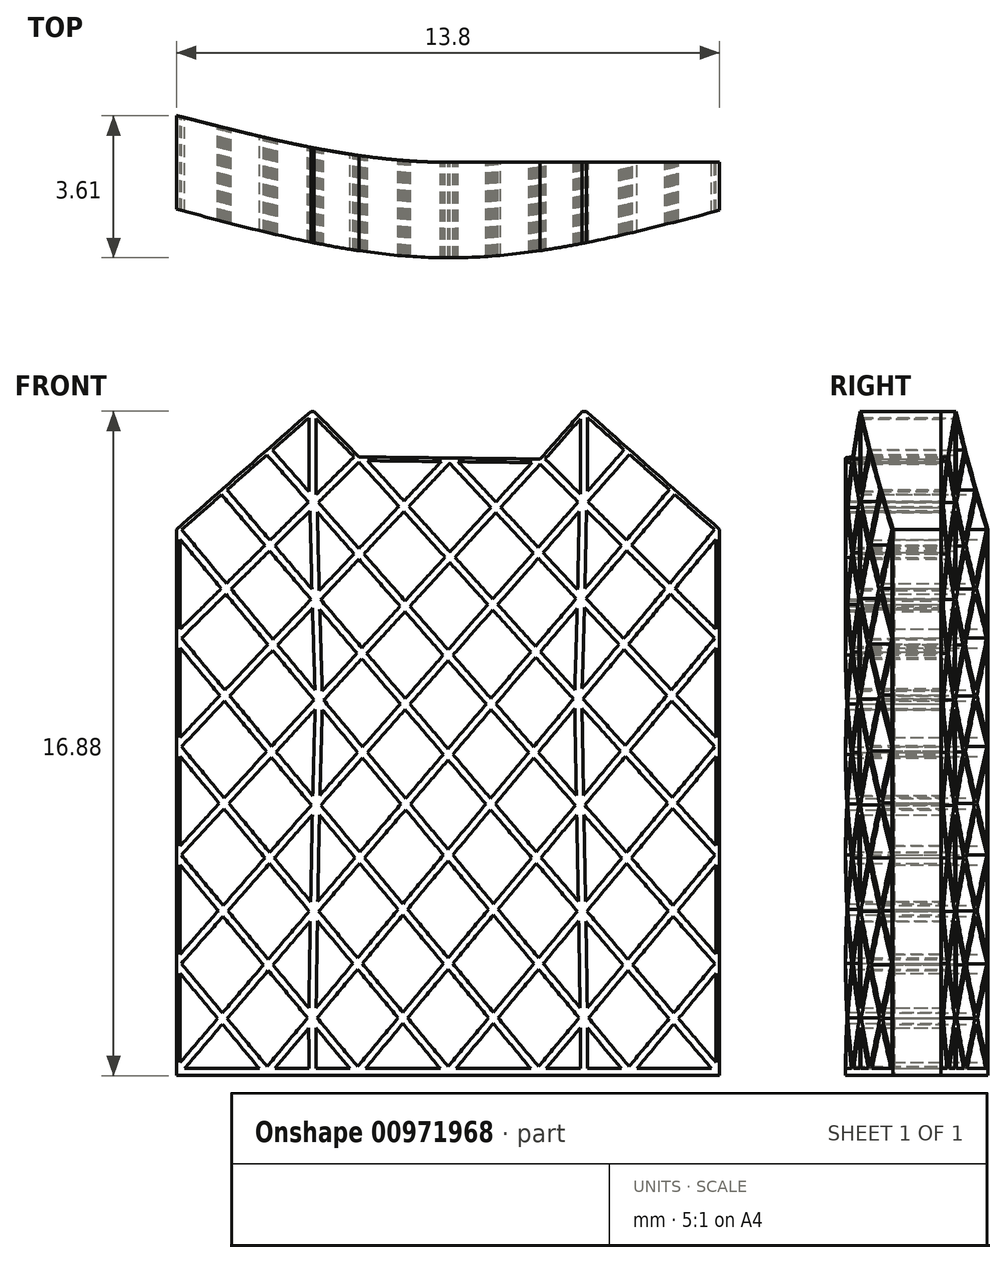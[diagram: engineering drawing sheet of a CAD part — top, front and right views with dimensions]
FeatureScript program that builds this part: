
annotation { "Feature Type Name" : "Feature", "Feature Type Description" : "" }
export const myFeature = defineFeature(function(context is Context, id is Id, definition is map)
    precondition{}
    {
        {
            var Q0;
            Q0=qCreatedBy(makeId("Top.planeOp"),FACE);
            var sketch = newSketch(context, id + "F0", { "sketchPlane" : qUnion([Q0])});
            skLineSegment(sketch, "E0", {"start": v(0, -22.65) * mm, "end": v(38.1, -22.65) * mm});
            skLineSegment(sketch, "E1", {"start": v(38.1, -22.65) * mm, "end": v(-38.1, -22.65) * mm});
            skLineSegment(sketch, "E2", {"start": v(38.1, -22.65) * mm, "end": v(38.1, -16.26) * mm});
            skLineSegment(sketch, "E3", {"start": v(38.1, -16.26) * mm, "end": v(38.1, -29.4) * mm});
            skLineSegment(sketch, "E4", {"start": v(-38.1, -22.65) * mm, "end": v(-38.1, -29.22) * mm});
            skLineSegment(sketch, "E5", {"start": v(-38.1, -29.22) * mm, "end": v(-38.1, -16.09) * mm});
            skPoint(sketch, "E6", {"position": v(-38.1, -22.65) * mm});
            skPoint(sketch, "E7", {"position": v(38.1, -22.82) * mm});
            skFitSpline(sketch, "E8", {"points": [v(-38.1, -16.09) * mm, v(0, -22.65) * mm, v(38.1, -16.26) * mm], "startDerivative": vector(76.18, -19.61) * mm, "endDerivative": vector(76.22, 19.27) * mm});
            skLineSegment(sketch, "E9", {"start": v(0, -22.65) * mm, "end": v(0, -36.06) * mm});
            skFitSpline(sketch, "E10", {"points": [v(-38.1, -29.22) * mm, v(0, -36.06) * mm, v(38.1, -29.4) * mm], "startDerivative": vector(76.18, -20.42) * mm, "endDerivative": vector(76.22, 20.08) * mm});
            skSolve(sketch);
        }
        {
            var Q0;
            Q0=qCreatedBy(makeId("Front.planeOp"),FACE);
            var sketch = newSketch(context, id + "F1", { "sketchPlane" : qUnion([Q0])});
            skLineSegment(sketch, "E11", {"start": v(38.1, -46.14) * mm, "end": v(25.4, -46.14) * mm, "construction": true});
            skLineSegment(sketch, "E12", {"start": v(-38.1, -46.14) * mm, "end": v(-38.1, -30.9) * mm, "construction": true});
            skLineSegment(sketch, "E13", {"start": v(38.1, 30.06) * mm, "end": v(38.1, 14.82) * mm, "construction": true});
            skLineSegment(sketch, "E14", {"start": v(-38.1, 30.06) * mm, "end": v(-31.74, 35.65) * mm, "construction": true});
            skLineSegment(sketch, "E15", {"start": v(38.1, 30.06) * mm, "end": v(31.76, 35.67) * mm, "construction": true});
            skLineSegment(sketch, "E16", {"start": v(-19.02, 46.83) * mm, "end": v(-12.48, 40.22) * mm, "construction": true});
            skLineSegment(sketch, "E17", {"start": v(19.08, 46.9) * mm, "end": v(12.92, 39.93) * mm, "construction": true});
            skLineSegment(sketch, "E18", {"start": v(-12.48, 40.22) * mm, "end": v(0.22, 40.07) * mm, "construction": true});
            skLineSegment(sketch, "E19", {"start": v(-25.38, 41.24) * mm, "end": v(-19.02, 46.83) * mm, "construction": true});
            skLineSegment(sketch, "E20", {"start": v(-31.74, 35.65) * mm, "end": v(-25.38, 41.24) * mm, "construction": true});
            skLineSegment(sketch, "E21", {"start": v(25.42, 41.28) * mm, "end": v(19.08, 46.9) * mm, "construction": true});
            skLineSegment(sketch, "E22", {"start": v(31.76, 35.67) * mm, "end": v(25.42, 41.28) * mm, "construction": true});
            skLineSegment(sketch, "E23", {"start": v(38.1, 14.82) * mm, "end": v(38.1, -0.42) * mm, "construction": true});
            skLineSegment(sketch, "E24", {"start": v(38.1, -0.42) * mm, "end": v(38.1, -15.66) * mm, "construction": true});
            skLineSegment(sketch, "E25", {"start": v(38.1, -15.66) * mm, "end": v(38.1, -30.9) * mm, "construction": true});
            skLineSegment(sketch, "E26", {"start": v(38.1, -30.9) * mm, "end": v(38.1, -46.14) * mm, "construction": true});
            skLineSegment(sketch, "E27", {"start": v(-38.1, 14.82) * mm, "end": v(-38.1, 30.06) * mm, "construction": true});
            skLineSegment(sketch, "E28", {"start": v(-38.1, -0.42) * mm, "end": v(-38.1, 14.82) * mm, "construction": true});
            skLineSegment(sketch, "E29", {"start": v(-38.1, -15.66) * mm, "end": v(-38.1, -0.42) * mm, "construction": true});
            skLineSegment(sketch, "E30", {"start": v(-38.1, -30.9) * mm, "end": v(-38.1, -15.66) * mm, "construction": true});
            skLineSegment(sketch, "E31", {"start": v(-25.4, -46.14) * mm, "end": v(-38.1, -46.14) * mm, "construction": true});
            skLineSegment(sketch, "E32", {"start": v(-12.7, -46.14) * mm, "end": v(-19.02, -46.14) * mm, "construction": true});
            skLineSegment(sketch, "E33", {"start": v(-50.8, 0) * mm, "end": v(-50.8, 0) * mm});
            skLineSegment(sketch, "E34", {"start": v(12.7, -46.14) * mm, "end": v(0, -46.14) * mm, "construction": true});
            skLineSegment(sketch, "E35", {"start": v(25.4, -46.14) * mm, "end": v(19.08, -46.14) * mm, "construction": true});
            skLineSegment(sketch, "E36", {"start": v(0, -46.14) * mm, "end": v(-12.7, -46.14) * mm, "construction": true});
            skLineSegment(sketch, "E37", {"start": v(12.92, 39.93) * mm, "end": v(18.94, 33.92) * mm, "construction": true});
            skPoint(sketch, "E38", {"position": v(0.22, 40.07) * mm});
            skLineSegment(sketch, "E39", {"start": v(-12.48, 40.22) * mm, "end": v(-6.2, 33.29) * mm, "construction": true});
            skLineSegment(sketch, "E40", {"start": v(0.22, 40.07) * mm, "end": v(6.7, 33.15) * mm, "construction": true});
            skLineSegment(sketch, "E41", {"start": v(-25.38, 41.24) * mm, "end": v(-19.02, 34.01) * mm, "construction": true});
            skLineSegment(sketch, "E42", {"start": v(-31.74, 35.65) * mm, "end": v(-25.02, 27.78) * mm, "construction": true});
            skLineSegment(sketch, "E43", {"start": v(-38.1, 30.06) * mm, "end": v(-31.15, 21.71) * mm, "construction": true});
            skLineSegment(sketch, "E44", {"start": v(-38.1, -0.42) * mm, "end": v(-31.44, -8.4) * mm, "construction": true});
            skLineSegment(sketch, "E45", {"start": v(-38.1, -15.66) * mm, "end": v(-31.58, -23.49) * mm, "construction": true});
            skLineSegment(sketch, "E46", {"start": v(-38.1, -30.9) * mm, "end": v(-31.67, -38.62) * mm, "construction": true});
            skLineSegment(sketch, "E47", {"start": v(-12.48, 40.22) * mm, "end": v(-18.9, 33.86) * mm, "construction": true});
            skLineSegment(sketch, "E48", {"start": v(0.22, 40.07) * mm, "end": v(-6.2, 33.29) * mm, "construction": true});
            skLineSegment(sketch, "E49", {"start": v(12.92, 39.93) * mm, "end": v(6.7, 33.15) * mm, "construction": true});
            skLineSegment(sketch, "E50", {"start": v(25.42, 41.28) * mm, "end": v(19.08, 34.07) * mm, "construction": true});
            skLineSegment(sketch, "E51", {"start": v(31.76, 35.67) * mm, "end": v(25.06, 27.82) * mm, "construction": true});
            skLineSegment(sketch, "E52", {"start": v(38.1, 30.06) * mm, "end": v(31.16, 21.73) * mm, "construction": true});
            skLineSegment(sketch, "E53", {"start": v(38.1, 14.82) * mm, "end": v(31.38, 6.76) * mm, "construction": true});
            skLineSegment(sketch, "E54", {"start": v(38.1, -0.42) * mm, "end": v(31.49, -8.36) * mm, "construction": true});
            skLineSegment(sketch, "E55", {"start": v(38.1, -30.9) * mm, "end": v(31.67, -38.61) * mm, "construction": true});
            skLineSegment(sketch, "E56", {"start": v(-38.1, 14.82) * mm, "end": v(-31.35, 6.71) * mm, "construction": true});
            skLineSegment(sketch, "E57", {"start": v(38.1, -15.66) * mm, "end": v(31.58, -23.49) * mm, "construction": true});
            skLineSegment(sketch, "E58", {"start": v(0.22, 40.07) * mm, "end": v(12.92, 39.93) * mm, "construction": true});
            skLineSegment(sketch, "E59", {"start": v(19.08, 34.07) * mm, "end": v(18.94, 33.92) * mm, "construction": true});
            skLineSegment(sketch, "E60", {"start": v(18.94, 33.92) * mm, "end": v(19.08, 33.79) * mm, "construction": true});
            skLineSegment(sketch, "E61", {"start": v(19.08, 33.79) * mm, "end": v(25.06, 27.82) * mm, "construction": true});
            skLineSegment(sketch, "E62", {"start": v(18.67, 20.34) * mm, "end": v(12.28, 12.86) * mm, "construction": true});
            skLineSegment(sketch, "E63", {"start": v(18.53, -8.66) * mm, "end": v(12.4, -16.03) * mm, "construction": true});
            skLineSegment(sketch, "E64", {"start": v(18.82, -23.56) * mm, "end": v(12.7, -30.9) * mm, "construction": true});
            skLineSegment(sketch, "E65", {"start": v(19.08, -46.14) * mm, "end": v(12.7, -46.14) * mm, "construction": true});
            skLineSegment(sketch, "E66", {"start": v(18.94, 33.92) * mm, "end": v(12.66, 26.78) * mm, "construction": true});
            skLineSegment(sketch, "E67", {"start": v(25.06, 27.82) * mm, "end": v(18.67, 20.34) * mm, "construction": true});
            skLineSegment(sketch, "E68", {"start": v(25.06, 27.82) * mm, "end": v(31.16, 21.73) * mm, "construction": true});
            skLineSegment(sketch, "E69", {"start": v(31.16, 21.73) * mm, "end": v(24.67, 13.94) * mm, "construction": true});
            skLineSegment(sketch, "E70", {"start": v(31.16, 21.73) * mm, "end": v(38.1, 14.82) * mm, "construction": true});
            skLineSegment(sketch, "E71.0", {"start": v(24.7, 41.23) * mm, "end": v(19.59, 45.76) * mm});
            skLineSegment(sketch, "E71.1", {"start": v(24.7, 41.23) * mm, "end": v(19.59, 35.43) * mm});
            skLineSegment(sketch, "E71.2", {"start": v(19.59, 45.76) * mm, "end": v(19.59, 35.43) * mm});
            skLineSegment(sketch, "E72.0", {"start": v(18.56, 45.52) * mm, "end": v(18.56, 35.03) * mm});
            skLineSegment(sketch, "E72.1", {"start": v(18.56, 45.52) * mm, "end": v(13.63, 39.95) * mm});
            skLineSegment(sketch, "E72.2", {"start": v(13.63, 39.95) * mm, "end": v(18.56, 35.03) * mm});
            skLineSegment(sketch, "E73.0", {"start": v(31.05, 35.62) * mm, "end": v(25.46, 40.56) * mm});
            skLineSegment(sketch, "E73.1", {"start": v(31.05, 35.62) * mm, "end": v(25.03, 28.57) * mm});
            skLineSegment(sketch, "E73.2", {"start": v(19.64, 33.94) * mm, "end": v(25.03, 28.57) * mm});
            skLineSegment(sketch, "E73.3", {"start": v(25.46, 40.56) * mm, "end": v(19.64, 33.94) * mm});
            skLineSegment(sketch, "E74.0", {"start": v(37.4, 30) * mm, "end": v(31.8, 34.95) * mm});
            skLineSegment(sketch, "E74.1", {"start": v(37.4, 30) * mm, "end": v(31.13, 22.49) * mm});
            skLineSegment(sketch, "E74.2", {"start": v(25.75, 27.85) * mm, "end": v(31.13, 22.49) * mm});
            skLineSegment(sketch, "E74.3", {"start": v(31.8, 34.95) * mm, "end": v(25.75, 27.85) * mm});
            skLineSegment(sketch, "E75.0", {"start": v(37.6, 28.65) * mm, "end": v(37.6, 16.04) * mm});
            skLineSegment(sketch, "E75.1", {"start": v(37.6, 28.65) * mm, "end": v(31.85, 21.77) * mm});
            skLineSegment(sketch, "E75.2", {"start": v(31.85, 21.77) * mm, "end": v(37.6, 16.04) * mm});
            skLineSegment(sketch, "E76", {"start": v(-19.02, 34.01) * mm, "end": v(-18.9, 33.86) * mm, "construction": true});
            skLineSegment(sketch, "E77", {"start": v(-18.9, 33.86) * mm, "end": v(-19.02, 33.73) * mm, "construction": true});
            skLineSegment(sketch, "E78", {"start": v(-18.9, 33.86) * mm, "end": v(-12.52, 26.62) * mm, "construction": true});
            skLineSegment(sketch, "E79", {"start": v(-19.02, 33.73) * mm, "end": v(-25.02, 27.78) * mm, "construction": true});
            skLineSegment(sketch, "E80", {"start": v(-18.57, 20.22) * mm, "end": v(-12.1, 12.66) * mm, "construction": true});
            skLineSegment(sketch, "E81", {"start": v(-18.57, 20.22) * mm, "end": v(-24.6, 13.85) * mm, "construction": true});
            skLineSegment(sketch, "E82", {"start": v(-18.13, 6.1) * mm, "end": v(-12, -1.25) * mm, "construction": true});
            skLineSegment(sketch, "E83", {"start": v(-18.13, 6.1) * mm, "end": v(-24.79, -1.16) * mm, "construction": true});
            skLineSegment(sketch, "E84", {"start": v(-18.82, -23.56) * mm, "end": v(-12.7, -30.9) * mm, "construction": true});
            skLineSegment(sketch, "E85", {"start": v(-18.82, -23.56) * mm, "end": v(-25.25, -31.09) * mm, "construction": true});
            skLineSegment(sketch, "E86", {"start": v(-19.05, -38.52) * mm, "end": v(-12.7, -46.14) * mm, "construction": true});
            skLineSegment(sketch, "E87", {"start": v(-19.05, -38.52) * mm, "end": v(-25.4, -46.14) * mm, "construction": true});
            skLineSegment(sketch, "E88", {"start": v(-19.02, -46.14) * mm, "end": v(-25.4, -46.14) * mm, "construction": true});
            skLineSegment(sketch, "E89", {"start": v(-25.02, 27.78) * mm, "end": v(-18.57, 20.22) * mm, "construction": true});
            skLineSegment(sketch, "E90", {"start": v(-25.02, 27.78) * mm, "end": v(-31.15, 21.71) * mm, "construction": true});
            skLineSegment(sketch, "E91", {"start": v(-31.15, 21.71) * mm, "end": v(-24.6, 13.85) * mm, "construction": true});
            skLineSegment(sketch, "E92", {"start": v(-31.15, 21.71) * mm, "end": v(-38.1, 14.82) * mm, "construction": true});
            skLineSegment(sketch, "E93.0", {"start": v(-37.4, 30) * mm, "end": v(-31.8, 34.93) * mm});
            skLineSegment(sketch, "E93.1", {"start": v(-37.4, 30) * mm, "end": v(-31.11, 22.46) * mm});
            skLineSegment(sketch, "E93.2", {"start": v(-25.72, 27.81) * mm, "end": v(-31.11, 22.46) * mm});
            skLineSegment(sketch, "E93.3", {"start": v(-31.8, 34.93) * mm, "end": v(-25.72, 27.81) * mm});
            skLineSegment(sketch, "E94.0", {"start": v(-37.6, 28.65) * mm, "end": v(-31.83, 21.75) * mm});
            skLineSegment(sketch, "E94.1", {"start": v(-37.6, 16.04) * mm, "end": v(-37.6, 28.65) * mm});
            skLineSegment(sketch, "E94.2", {"start": v(-31.83, 21.75) * mm, "end": v(-37.6, 16.04) * mm});
            skLineSegment(sketch, "E95", {"start": v(-6.2, 33.29) * mm, "end": v(0.26, 26.14) * mm, "construction": true});
            skLineSegment(sketch, "E96", {"start": v(-6.2, 33.29) * mm, "end": v(-12.52, 26.62) * mm, "construction": true});
            skLineSegment(sketch, "E97", {"start": v(6.7, 33.15) * mm, "end": v(12.66, 26.78) * mm, "construction": true});
            skLineSegment(sketch, "E98", {"start": v(6.7, 33.15) * mm, "end": v(0.26, 26.14) * mm, "construction": true});
            skLineSegment(sketch, "E99.0", {"start": v(-11.32, 39.7) * mm, "end": v(-6.2, 34.03) * mm});
            skLineSegment(sketch, "E99.1", {"start": v(-11.32, 39.7) * mm, "end": v(-0.95, 39.58) * mm});
            skLineSegment(sketch, "E99.2", {"start": v(-0.95, 39.58) * mm, "end": v(-6.2, 34.03) * mm});
            skLineSegment(sketch, "E100.0", {"start": v(1.4, 39.55) * mm, "end": v(11.77, 39.43) * mm});
            skLineSegment(sketch, "E100.1", {"start": v(1.4, 39.55) * mm, "end": v(6.7, 33.9) * mm});
            skLineSegment(sketch, "E100.2", {"start": v(11.77, 39.43) * mm, "end": v(6.7, 33.9) * mm});
            skLineSegment(sketch, "E101", {"start": v(0.26, 26.14) * mm, "end": v(-6.05, 19.26) * mm, "construction": true});
            skLineSegment(sketch, "E102", {"start": v(0.26, 26.14) * mm, "end": v(6.26, 19.51) * mm, "construction": true});
            skLineSegment(sketch, "E103", {"start": v(-12.52, 26.62) * mm, "end": v(-18.57, 20.22) * mm, "construction": true});
            skLineSegment(sketch, "E104", {"start": v(-6.05, 19.26) * mm, "end": v(-12.1, 12.66) * mm, "construction": true});
            skLineSegment(sketch, "E105", {"start": v(-6.05, 19.26) * mm, "end": v(0, 12.4) * mm, "construction": true});
            skLineSegment(sketch, "E106", {"start": v(-12.52, 26.62) * mm, "end": v(-6.05, 19.26) * mm, "construction": true});
            skLineSegment(sketch, "E107", {"start": v(12.66, 26.78) * mm, "end": v(18.67, 20.34) * mm, "construction": true});
            skLineSegment(sketch, "E108", {"start": v(12.66, 26.78) * mm, "end": v(6.26, 19.51) * mm, "construction": true});
            skLineSegment(sketch, "E109", {"start": v(6.26, 19.51) * mm, "end": v(0, 12.4) * mm, "construction": true});
            skLineSegment(sketch, "E110", {"start": v(6.26, 19.51) * mm, "end": v(12.28, 12.86) * mm, "construction": true});
            skLineSegment(sketch, "E111.0", {"start": v(12.93, 39.2) * mm, "end": v(18.25, 33.9) * mm});
            skLineSegment(sketch, "E111.1", {"start": v(12.93, 39.2) * mm, "end": v(7.39, 33.15) * mm});
            skLineSegment(sketch, "E111.2", {"start": v(7.39, 33.15) * mm, "end": v(12.65, 27.53) * mm});
            skLineSegment(sketch, "E111.3", {"start": v(18.25, 33.9) * mm, "end": v(12.65, 27.53) * mm});
            skLineSegment(sketch, "E112.0", {"start": v(6.7, 32.4) * mm, "end": v(11.97, 26.77) * mm});
            skLineSegment(sketch, "E112.1", {"start": v(6.7, 32.4) * mm, "end": v(0.95, 26.14) * mm});
            skLineSegment(sketch, "E112.2", {"start": v(0.95, 26.14) * mm, "end": v(6.26, 20.27) * mm});
            skLineSegment(sketch, "E112.3", {"start": v(11.97, 26.77) * mm, "end": v(6.26, 20.27) * mm});
            skLineSegment(sketch, "E113.0", {"start": v(0.22, 39.33) * mm, "end": v(6, 33.15) * mm});
            skLineSegment(sketch, "E113.1", {"start": v(0.22, 39.33) * mm, "end": v(-5.51, 33.28) * mm});
            skLineSegment(sketch, "E113.2", {"start": v(-5.51, 33.28) * mm, "end": v(0.27, 26.9) * mm});
            skLineSegment(sketch, "E113.3", {"start": v(6, 33.15) * mm, "end": v(0.27, 26.9) * mm});
            skLineSegment(sketch, "E114.0", {"start": v(-6.21, 32.54) * mm, "end": v(-0.42, 26.14) * mm});
            skLineSegment(sketch, "E114.1", {"start": v(-6.21, 32.54) * mm, "end": v(-11.83, 26.6) * mm});
            skLineSegment(sketch, "E114.2", {"start": v(-11.83, 26.6) * mm, "end": v(-6.04, 20.02) * mm});
            skLineSegment(sketch, "E114.3", {"start": v(-0.42, 26.14) * mm, "end": v(-6.04, 20.02) * mm});
            skLineSegment(sketch, "E115.0", {"start": v(-6.9, 33.3) * mm, "end": v(-12.5, 27.37) * mm});
            skLineSegment(sketch, "E115.1", {"start": v(-12.5, 39.49) * mm, "end": v(-6.9, 33.3) * mm});
            skLineSegment(sketch, "E115.2", {"start": v(-12.5, 39.49) * mm, "end": v(-18.2, 33.84) * mm});
            skLineSegment(sketch, "E115.3", {"start": v(-18.2, 33.84) * mm, "end": v(-12.5, 27.37) * mm});
            skLineSegment(sketch, "E116.0", {"start": v(-18.51, 45.6) * mm, "end": v(-13.2, 40.22) * mm});
            skLineSegment(sketch, "E116.1", {"start": v(-18.51, 45.6) * mm, "end": v(-18.51, 34.95) * mm});
            skLineSegment(sketch, "E116.2", {"start": v(-13.2, 40.22) * mm, "end": v(-18.51, 34.95) * mm});
            skLineSegment(sketch, "E117.0", {"start": v(-19.53, 45.7) * mm, "end": v(-19.53, 35.36) * mm});
            skLineSegment(sketch, "E117.1", {"start": v(-24.66, 41.2) * mm, "end": v(-19.53, 45.7) * mm});
            skLineSegment(sketch, "E117.2", {"start": v(-24.66, 41.2) * mm, "end": v(-19.53, 35.36) * mm});
            skLineSegment(sketch, "E118.0", {"start": v(-25.43, 40.52) * mm, "end": v(-19.59, 33.89) * mm});
            skLineSegment(sketch, "E118.1", {"start": v(-31.03, 35.6) * mm, "end": v(-25.43, 40.52) * mm});
            skLineSegment(sketch, "E118.2", {"start": v(-31.03, 35.6) * mm, "end": v(-25, 28.53) * mm});
            skLineSegment(sketch, "E118.3", {"start": v(-19.59, 33.89) * mm, "end": v(-25, 28.53) * mm});
            skLineSegment(sketch, "E119", {"start": v(31.38, 6.76) * mm, "end": v(24.88, -1.05) * mm, "construction": true});
            skLineSegment(sketch, "E120", {"start": v(31.38, 6.76) * mm, "end": v(38.1, -0.42) * mm, "construction": true});
            skLineSegment(sketch, "E121", {"start": v(31.49, -8.36) * mm, "end": v(25.05, -16.08) * mm, "construction": true});
            skLineSegment(sketch, "E122", {"start": v(31.49, -8.36) * mm, "end": v(38.1, -15.66) * mm, "construction": true});
            skLineSegment(sketch, "E123", {"start": v(31.58, -23.49) * mm, "end": v(25.24, -31.09) * mm, "construction": true});
            skLineSegment(sketch, "E124", {"start": v(31.58, -23.49) * mm, "end": v(38.1, -30.9) * mm, "construction": true});
            skLineSegment(sketch, "E125", {"start": v(31.67, -38.61) * mm, "end": v(25.4, -46.14) * mm, "construction": true});
            skLineSegment(sketch, "E126", {"start": v(31.67, -38.61) * mm, "end": v(38.1, -46.14) * mm, "construction": true});
            skLineSegment(sketch, "E127.0", {"start": v(37.6, 13.43) * mm, "end": v(32.05, 6.78) * mm});
            skLineSegment(sketch, "E127.1", {"start": v(37.6, 13.43) * mm, "end": v(37.6, 0.85) * mm});
            skLineSegment(sketch, "E127.2", {"start": v(32.05, 6.78) * mm, "end": v(37.6, 0.85) * mm});
            skLineSegment(sketch, "E128.0", {"start": v(37.6, -1.83) * mm, "end": v(32.16, -8.34) * mm});
            skLineSegment(sketch, "E128.1", {"start": v(37.6, -1.83) * mm, "end": v(37.6, -14.34) * mm});
            skLineSegment(sketch, "E128.2", {"start": v(32.16, -8.34) * mm, "end": v(37.6, -14.34) * mm});
            skLineSegment(sketch, "E129.0", {"start": v(37.6, -17.07) * mm, "end": v(32.25, -23.48) * mm});
            skLineSegment(sketch, "E129.1", {"start": v(37.6, -17.07) * mm, "end": v(37.6, -29.56) * mm});
            skLineSegment(sketch, "E129.2", {"start": v(32.25, -23.48) * mm, "end": v(37.6, -29.56) * mm});
            skLineSegment(sketch, "E130.0", {"start": v(37.6, -32.3) * mm, "end": v(32.34, -38.61) * mm});
            skLineSegment(sketch, "E130.1", {"start": v(37.6, -32.3) * mm, "end": v(37.6, -44.76) * mm});
            skLineSegment(sketch, "E130.2", {"start": v(32.34, -38.61) * mm, "end": v(37.6, -44.76) * mm});
            skLineSegment(sketch, "E131", {"start": v(-31.35, 6.71) * mm, "end": v(-24.79, -1.16) * mm, "construction": true});
            skLineSegment(sketch, "E132", {"start": v(-31.35, 6.71) * mm, "end": v(-38.1, -0.42) * mm, "construction": true});
            skLineSegment(sketch, "E133", {"start": v(-31.44, -8.4) * mm, "end": v(-25.05, -16.08) * mm, "construction": true});
            skLineSegment(sketch, "E134", {"start": v(-31.44, -8.4) * mm, "end": v(-38.1, -15.66) * mm, "construction": true});
            skLineSegment(sketch, "E135", {"start": v(-31.58, -23.49) * mm, "end": v(-25.25, -31.09) * mm, "construction": true});
            skLineSegment(sketch, "E136", {"start": v(-31.58, -23.49) * mm, "end": v(-38.1, -30.9) * mm, "construction": true});
            skLineSegment(sketch, "E137", {"start": v(-31.67, -38.62) * mm, "end": v(-38.1, -46.14) * mm, "construction": true});
            skLineSegment(sketch, "E138", {"start": v(-31.67, -38.62) * mm, "end": v(-25.4, -46.14) * mm, "construction": true});
            skLineSegment(sketch, "E139.0", {"start": v(-37.6, 13.41) * mm, "end": v(-32.03, 6.74) * mm});
            skLineSegment(sketch, "E139.1", {"start": v(-37.6, 0.85) * mm, "end": v(-37.6, 13.41) * mm});
            skLineSegment(sketch, "E139.2", {"start": v(-32.03, 6.74) * mm, "end": v(-37.6, 0.85) * mm});
            skLineSegment(sketch, "E140.0", {"start": v(-37.6, -1.83) * mm, "end": v(-32.12, -8.4) * mm});
            skLineSegment(sketch, "E140.1", {"start": v(-37.6, -14.36) * mm, "end": v(-37.6, -1.83) * mm});
            skLineSegment(sketch, "E140.2", {"start": v(-32.12, -8.4) * mm, "end": v(-37.6, -14.36) * mm});
            skLineSegment(sketch, "E141.0", {"start": v(-37.6, -17.04) * mm, "end": v(-32.24, -23.48) * mm});
            skLineSegment(sketch, "E141.1", {"start": v(-37.6, -29.58) * mm, "end": v(-37.6, -17.04) * mm});
            skLineSegment(sketch, "E141.2", {"start": v(-32.24, -23.48) * mm, "end": v(-37.6, -29.58) * mm});
            skLineSegment(sketch, "E142.0", {"start": v(-37.6, -44.78) * mm, "end": v(-37.6, -32.3) * mm});
            skLineSegment(sketch, "E142.1", {"start": v(-32.33, -38.61) * mm, "end": v(-37.6, -44.78) * mm});
            skLineSegment(sketch, "E142.2", {"start": v(-37.6, -32.3) * mm, "end": v(-32.33, -38.61) * mm});
            skLineSegment(sketch, "E143.0", {"start": v(-31.68, -39.4) * mm, "end": v(-37, -45.63) * mm});
            skLineSegment(sketch, "E143.1", {"start": v(-31.68, -39.4) * mm, "end": v(-26.48, -45.63) * mm});
            skLineSegment(sketch, "E143.2", {"start": v(-26.48, -45.63) * mm, "end": v(-37, -45.63) * mm});
            skLineSegment(sketch, "E144", {"start": v(-6.35, -38.52) * mm, "end": v(0, -46.14) * mm, "construction": true});
            skLineSegment(sketch, "E145", {"start": v(-6.35, -38.52) * mm, "end": v(-12.7, -46.14) * mm, "construction": true});
            skLineSegment(sketch, "E146.0", {"start": v(-6.35, -39.32) * mm, "end": v(-11.62, -45.63) * mm});
            skLineSegment(sketch, "E146.1", {"start": v(-6.35, -39.32) * mm, "end": v(-1.08, -45.63) * mm});
            skLineSegment(sketch, "E146.2", {"start": v(-1.08, -45.63) * mm, "end": v(-11.62, -45.63) * mm});
            skLineSegment(sketch, "E147.0", {"start": v(37, -45.63) * mm, "end": v(26.48, -45.63) * mm});
            skLineSegment(sketch, "E147.1", {"start": v(31.68, -39.4) * mm, "end": v(37, -45.63) * mm});
            skLineSegment(sketch, "E147.2", {"start": v(31.68, -39.4) * mm, "end": v(26.48, -45.63) * mm});
            skLineSegment(sketch, "E148", {"start": v(-24.6, 13.85) * mm, "end": v(-18.13, 6.1) * mm, "construction": true});
            skLineSegment(sketch, "E149", {"start": v(-24.6, 13.85) * mm, "end": v(-31.35, 6.71) * mm, "construction": true});
            skLineSegment(sketch, "E150", {"start": v(-24.79, -1.16) * mm, "end": v(-31.44, -8.4) * mm, "construction": true});
            skLineSegment(sketch, "E151", {"start": v(-25.05, -16.08) * mm, "end": v(-18.82, -23.56) * mm, "construction": true});
            skLineSegment(sketch, "E152", {"start": v(-25.05, -16.08) * mm, "end": v(-31.58, -23.49) * mm, "construction": true});
            skLineSegment(sketch, "E153", {"start": v(-25.25, -31.09) * mm, "end": v(-31.67, -38.62) * mm, "construction": true});
            skLineSegment(sketch, "E154", {"start": v(-25.25, -31.09) * mm, "end": v(-19.05, -38.52) * mm, "construction": true});
            skLineSegment(sketch, "E155.0", {"start": v(-31.18, 20.96) * mm, "end": v(-25.27, 13.87) * mm});
            skLineSegment(sketch, "E155.1", {"start": v(-31.18, 20.96) * mm, "end": v(-37.41, 14.79) * mm});
            skLineSegment(sketch, "E155.2", {"start": v(-37.41, 14.79) * mm, "end": v(-31.32, 7.48) * mm});
            skLineSegment(sketch, "E155.3", {"start": v(-25.27, 13.87) * mm, "end": v(-31.32, 7.48) * mm});
            skLineSegment(sketch, "E156", {"start": v(-24.79, -1.16) * mm, "end": v(-18.53, -8.66) * mm, "construction": true});
            skLineSegment(sketch, "E157.0", {"start": v(-31.37, 5.95) * mm, "end": v(-25.46, -1.14) * mm});
            skLineSegment(sketch, "E157.1", {"start": v(-31.37, 5.95) * mm, "end": v(-37.42, -0.44) * mm});
            skLineSegment(sketch, "E157.2", {"start": v(-37.42, -0.44) * mm, "end": v(-31.43, -7.64) * mm});
            skLineSegment(sketch, "E157.3", {"start": v(-25.46, -1.14) * mm, "end": v(-31.43, -7.64) * mm});
            skLineSegment(sketch, "E158.0", {"start": v(-31.46, -9.17) * mm, "end": v(-25.7, -16.07) * mm});
            skLineSegment(sketch, "E158.1", {"start": v(-31.46, -9.17) * mm, "end": v(-37.44, -15.68) * mm});
            skLineSegment(sketch, "E158.2", {"start": v(-37.44, -15.68) * mm, "end": v(-31.57, -22.72) * mm});
            skLineSegment(sketch, "E158.3", {"start": v(-25.7, -16.07) * mm, "end": v(-31.57, -22.72) * mm});
            skLineSegment(sketch, "E159.0", {"start": v(-31.59, -24.27) * mm, "end": v(-25.91, -31.08) * mm});
            skLineSegment(sketch, "E159.1", {"start": v(-31.59, -24.27) * mm, "end": v(-37.43, -30.91) * mm});
            skLineSegment(sketch, "E159.2", {"start": v(-37.43, -30.91) * mm, "end": v(-31.67, -37.82) * mm});
            skLineSegment(sketch, "E159.3", {"start": v(-25.91, -31.08) * mm, "end": v(-31.67, -37.82) * mm});
            skLineSegment(sketch, "E160", {"start": v(24.67, 13.94) * mm, "end": v(31.38, 6.76) * mm, "construction": true});
            skLineSegment(sketch, "E161", {"start": v(24.88, -1.05) * mm, "end": v(18.53, -8.66) * mm, "construction": true});
            skLineSegment(sketch, "E162", {"start": v(24.88, -1.05) * mm, "end": v(31.49, -8.36) * mm, "construction": true});
            skLineSegment(sketch, "E163", {"start": v(25.05, -16.08) * mm, "end": v(18.82, -23.56) * mm, "construction": true});
            skLineSegment(sketch, "E164", {"start": v(25.05, -16.08) * mm, "end": v(31.58, -23.49) * mm, "construction": true});
            skLineSegment(sketch, "E165", {"start": v(25.24, -31.09) * mm, "end": v(31.67, -38.61) * mm, "construction": true});
            skLineSegment(sketch, "E166.0", {"start": v(31.2, 20.98) * mm, "end": v(25.34, 13.96) * mm});
            skLineSegment(sketch, "E166.1", {"start": v(31.2, 20.98) * mm, "end": v(37.41, 14.79) * mm});
            skLineSegment(sketch, "E166.2", {"start": v(37.41, 14.79) * mm, "end": v(31.36, 7.53) * mm});
            skLineSegment(sketch, "E166.3", {"start": v(25.34, 13.96) * mm, "end": v(31.36, 7.53) * mm});
            skLineSegment(sketch, "E167.0", {"start": v(31.4, 6) * mm, "end": v(25.55, -1.04) * mm});
            skLineSegment(sketch, "E167.1", {"start": v(31.4, 6) * mm, "end": v(37.42, -0.44) * mm});
            skLineSegment(sketch, "E167.2", {"start": v(37.42, -0.44) * mm, "end": v(31.47, -7.58) * mm});
            skLineSegment(sketch, "E167.3", {"start": v(25.55, -1.04) * mm, "end": v(31.47, -7.58) * mm});
            skLineSegment(sketch, "E168.0", {"start": v(31.5, -9.13) * mm, "end": v(25.72, -16.07) * mm});
            skLineSegment(sketch, "E168.1", {"start": v(31.5, -9.13) * mm, "end": v(37.43, -15.68) * mm});
            skLineSegment(sketch, "E168.2", {"start": v(37.43, -15.68) * mm, "end": v(31.57, -22.7) * mm});
            skLineSegment(sketch, "E168.3", {"start": v(25.72, -16.07) * mm, "end": v(31.57, -22.7) * mm});
            skLineSegment(sketch, "E169.0", {"start": v(31.59, -24.27) * mm, "end": v(25.9, -31.08) * mm});
            skLineSegment(sketch, "E169.1", {"start": v(31.59, -24.27) * mm, "end": v(37.43, -30.91) * mm});
            skLineSegment(sketch, "E169.2", {"start": v(37.43, -30.91) * mm, "end": v(31.67, -37.83) * mm});
            skLineSegment(sketch, "E169.3", {"start": v(25.9, -31.08) * mm, "end": v(31.67, -37.83) * mm});
            skLineSegment(sketch, "E170", {"start": v(0, 12.4) * mm, "end": v(6.03, 5.54) * mm, "construction": true});
            skLineSegment(sketch, "E171", {"start": v(0, 12.4) * mm, "end": v(-6.03, 5.54) * mm, "construction": true});
            skLineSegment(sketch, "E172.0", {"start": v(-5.36, 19.26) * mm, "end": v(0, 13.16) * mm});
            skLineSegment(sketch, "E172.1", {"start": v(0.26, 25.39) * mm, "end": v(-5.36, 19.26) * mm});
            skLineSegment(sketch, "E172.2", {"start": v(0.26, 25.39) * mm, "end": v(5.58, 19.5) * mm});
            skLineSegment(sketch, "E172.3", {"start": v(5.58, 19.5) * mm, "end": v(0, 13.16) * mm});
            skLineSegment(sketch, "E173", {"start": v(-12.1, 12.66) * mm, "end": v(-18.13, 6.1) * mm, "construction": true});
            skLineSegment(sketch, "E174", {"start": v(-6.03, 5.54) * mm, "end": v(-12, -1.25) * mm, "construction": true});
            skLineSegment(sketch, "E175", {"start": v(-12.1, 12.66) * mm, "end": v(-6.03, 5.54) * mm, "construction": true});
            skLineSegment(sketch, "E176", {"start": v(-6.03, 5.54) * mm, "end": v(0, -1.52) * mm, "construction": true});
            skLineSegment(sketch, "E177", {"start": v(12.28, 12.86) * mm, "end": v(18.26, 6.25) * mm, "construction": true});
            skLineSegment(sketch, "E178", {"start": v(6.03, 5.54) * mm, "end": v(0, -1.52) * mm, "construction": true});
            skLineSegment(sketch, "E179", {"start": v(6.03, 5.54) * mm, "end": v(12, -1.25) * mm, "construction": true});
            skLineSegment(sketch, "E180", {"start": v(12.28, 12.86) * mm, "end": v(6.03, 5.54) * mm, "construction": true});
            skLineSegment(sketch, "E181.0", {"start": v(-6.05, 18.5) * mm, "end": v(-11.43, 12.65) * mm});
            skLineSegment(sketch, "E181.1", {"start": v(-6.05, 18.5) * mm, "end": v(-0.68, 12.4) * mm});
            skLineSegment(sketch, "E181.2", {"start": v(-0.68, 12.4) * mm, "end": v(-6.03, 6.32) * mm});
            skLineSegment(sketch, "E181.3", {"start": v(-11.43, 12.65) * mm, "end": v(-6.03, 6.32) * mm});
            skLineSegment(sketch, "E182.0", {"start": v(6.27, 18.75) * mm, "end": v(0.68, 12.4) * mm});
            skLineSegment(sketch, "E182.1", {"start": v(6.27, 18.75) * mm, "end": v(11.6, 12.85) * mm});
            skLineSegment(sketch, "E182.2", {"start": v(11.6, 12.85) * mm, "end": v(6.03, 6.32) * mm});
            skLineSegment(sketch, "E182.3", {"start": v(0.68, 12.4) * mm, "end": v(6.03, 6.32) * mm});
            skLineSegment(sketch, "E183", {"start": v(0, -1.52) * mm, "end": v(-5.96, -8.5) * mm, "construction": true});
            skLineSegment(sketch, "E184", {"start": v(0, -1.52) * mm, "end": v(5.96, -8.5) * mm, "construction": true});
            skLineSegment(sketch, "E185.0", {"start": v(0, 11.63) * mm, "end": v(-5.36, 5.53) * mm});
            skLineSegment(sketch, "E185.1", {"start": v(0, 11.63) * mm, "end": v(5.36, 5.53) * mm});
            skLineSegment(sketch, "E185.2", {"start": v(5.36, 5.53) * mm, "end": v(0, -0.74) * mm});
            skLineSegment(sketch, "E185.3", {"start": v(-5.36, 5.53) * mm, "end": v(0, -0.74) * mm});
            skLineSegment(sketch, "E186", {"start": v(5.96, -8.5) * mm, "end": v(12.4, -16.03) * mm, "construction": true});
            skLineSegment(sketch, "E187", {"start": v(12, -1.25) * mm, "end": v(18.53, -8.66) * mm, "construction": true});
            skLineSegment(sketch, "E188", {"start": v(12, -1.25) * mm, "end": v(5.96, -8.5) * mm, "construction": true});
            skLineSegment(sketch, "E189", {"start": v(5.96, -8.5) * mm, "end": v(0, -15.66) * mm, "construction": true});
            skLineSegment(sketch, "E190.0", {"start": v(6.04, 4.76) * mm, "end": v(0.67, -1.52) * mm});
            skLineSegment(sketch, "E190.1", {"start": v(6.04, 4.76) * mm, "end": v(11.34, -1.26) * mm});
            skLineSegment(sketch, "E190.2", {"start": v(11.34, -1.26) * mm, "end": v(5.96, -7.72) * mm});
            skLineSegment(sketch, "E190.3", {"start": v(0.67, -1.52) * mm, "end": v(5.96, -7.72) * mm});
            skLineSegment(sketch, "E191", {"start": v(-12, -1.25) * mm, "end": v(-18.53, -8.66) * mm, "construction": true});
            skLineSegment(sketch, "E192", {"start": v(-12, -1.25) * mm, "end": v(-5.96, -8.5) * mm, "construction": true});
            skLineSegment(sketch, "E193", {"start": v(-5.96, -8.5) * mm, "end": v(0, -15.66) * mm, "construction": true});
            skLineSegment(sketch, "E194", {"start": v(-5.96, -8.5) * mm, "end": v(-12.4, -16.03) * mm, "construction": true});
            skLineSegment(sketch, "E195.0", {"start": v(-6.04, 4.76) * mm, "end": v(-11.34, -1.26) * mm});
            skLineSegment(sketch, "E195.1", {"start": v(-6.04, 4.76) * mm, "end": v(-0.67, -1.52) * mm});
            skLineSegment(sketch, "E195.2", {"start": v(-0.67, -1.52) * mm, "end": v(-5.96, -7.72) * mm});
            skLineSegment(sketch, "E195.3", {"start": v(-11.34, -1.26) * mm, "end": v(-5.96, -7.72) * mm});
            skLineSegment(sketch, "E196", {"start": v(0, -15.66) * mm, "end": v(6.35, -23.28) * mm, "construction": true});
            skLineSegment(sketch, "E197", {"start": v(0, -15.66) * mm, "end": v(-6.35, -23.28) * mm, "construction": true});
            skLineSegment(sketch, "E198", {"start": v(12.4, -16.03) * mm, "end": v(18.82, -23.56) * mm, "construction": true});
            skLineSegment(sketch, "E199", {"start": v(6.35, -23.28) * mm, "end": v(0, -30.9) * mm, "construction": true});
            skLineSegment(sketch, "E200", {"start": v(6.35, -23.28) * mm, "end": v(12.7, -30.9) * mm, "construction": true});
            skLineSegment(sketch, "E201", {"start": v(-6.35, -23.28) * mm, "end": v(-12.7, -30.9) * mm, "construction": true});
            skLineSegment(sketch, "E202", {"start": v(-12.4, -16.03) * mm, "end": v(-18.82, -23.56) * mm, "construction": true});
            skLineSegment(sketch, "E203", {"start": v(-12.4, -16.03) * mm, "end": v(-6.35, -23.28) * mm, "construction": true});
            skLineSegment(sketch, "E204", {"start": v(-6.35, -23.28) * mm, "end": v(0, -30.9) * mm, "construction": true});
            skLineSegment(sketch, "E205.0", {"start": v(5.3, -8.51) * mm, "end": v(0, -14.87) * mm});
            skLineSegment(sketch, "E205.1", {"start": v(0, -2.3) * mm, "end": v(5.3, -8.51) * mm});
            skLineSegment(sketch, "E205.2", {"start": v(0, -2.3) * mm, "end": v(-5.3, -8.51) * mm});
            skLineSegment(sketch, "E205.3", {"start": v(-5.3, -8.51) * mm, "end": v(0, -14.87) * mm});
            skLineSegment(sketch, "E206", {"start": v(12.4, -16.03) * mm, "end": v(6.35, -23.28) * mm, "construction": true});
            skLineSegment(sketch, "E207.0", {"start": v(5.97, -9.3) * mm, "end": v(11.73, -16.04) * mm});
            skLineSegment(sketch, "E207.1", {"start": v(5.97, -9.3) * mm, "end": v(0.66, -15.66) * mm});
            skLineSegment(sketch, "E207.2", {"start": v(0.66, -15.66) * mm, "end": v(6.35, -22.49) * mm});
            skLineSegment(sketch, "E207.3", {"start": v(11.73, -16.04) * mm, "end": v(6.35, -22.49) * mm});
            skLineSegment(sketch, "E208.0", {"start": v(-5.97, -9.3) * mm, "end": v(-0.66, -15.66) * mm});
            skLineSegment(sketch, "E208.1", {"start": v(-5.97, -9.3) * mm, "end": v(-11.73, -16.04) * mm});
            skLineSegment(sketch, "E208.2", {"start": v(-11.73, -16.04) * mm, "end": v(-6.35, -22.49) * mm});
            skLineSegment(sketch, "E208.3", {"start": v(-0.66, -15.66) * mm, "end": v(-6.35, -22.49) * mm});
            skLineSegment(sketch, "E209", {"start": v(0, -30.9) * mm, "end": v(-6.35, -38.52) * mm, "construction": true});
            skLineSegment(sketch, "E210", {"start": v(0, -30.9) * mm, "end": v(6.35, -38.52) * mm, "construction": true});
            skLineSegment(sketch, "E211.0", {"start": v(0, -16.47) * mm, "end": v(-5.68, -23.28) * mm});
            skLineSegment(sketch, "E211.1", {"start": v(0, -16.47) * mm, "end": v(5.68, -23.28) * mm});
            skLineSegment(sketch, "E211.2", {"start": v(5.68, -23.28) * mm, "end": v(0, -30.1) * mm});
            skLineSegment(sketch, "E211.3", {"start": v(-5.68, -23.28) * mm, "end": v(0, -30.1) * mm});
            skLineSegment(sketch, "E212", {"start": v(-12.7, -30.9) * mm, "end": v(-19.05, -38.52) * mm, "construction": true});
            skLineSegment(sketch, "E213", {"start": v(-12.7, -30.9) * mm, "end": v(-6.35, -38.52) * mm, "construction": true});
            skLineSegment(sketch, "E214", {"start": v(12.7, -30.9) * mm, "end": v(19.05, -38.52) * mm, "construction": true});
            skLineSegment(sketch, "E215", {"start": v(12.7, -30.9) * mm, "end": v(6.35, -38.52) * mm, "construction": true});
            skLineSegment(sketch, "E216", {"start": v(6.35, -38.52) * mm, "end": v(0, -46.14) * mm, "construction": true});
            skLineSegment(sketch, "E217", {"start": v(6.35, -38.52) * mm, "end": v(12.7, -46.14) * mm, "construction": true});
            skLineSegment(sketch, "E218.0", {"start": v(-6.35, -24.08) * mm, "end": v(-0.66, -30.9) * mm});
            skLineSegment(sketch, "E218.1", {"start": v(-6.35, -24.08) * mm, "end": v(-12.04, -30.9) * mm});
            skLineSegment(sketch, "E218.2", {"start": v(-12.04, -30.9) * mm, "end": v(-6.35, -37.73) * mm});
            skLineSegment(sketch, "E218.3", {"start": v(-0.66, -30.9) * mm, "end": v(-6.35, -37.73) * mm});
            skLineSegment(sketch, "E219.0", {"start": v(6.35, -24.08) * mm, "end": v(0.66, -30.9) * mm});
            skLineSegment(sketch, "E219.1", {"start": v(6.35, -24.08) * mm, "end": v(12.04, -30.9) * mm});
            skLineSegment(sketch, "E219.2", {"start": v(12.04, -30.9) * mm, "end": v(6.35, -37.73) * mm});
            skLineSegment(sketch, "E219.3", {"start": v(0.66, -30.9) * mm, "end": v(6.35, -37.73) * mm});
            skLineSegment(sketch, "E220.0", {"start": v(0, -31.7) * mm, "end": v(5.69, -38.52) * mm});
            skLineSegment(sketch, "E220.1", {"start": v(0, -31.7) * mm, "end": v(-5.69, -38.52) * mm});
            skLineSegment(sketch, "E220.2", {"start": v(-5.69, -38.52) * mm, "end": v(0, -45.35) * mm});
            skLineSegment(sketch, "E220.3", {"start": v(5.69, -38.52) * mm, "end": v(0, -45.35) * mm});
            skLineSegment(sketch, "E221.0", {"start": v(12.67, 26) * mm, "end": v(17.98, 20.33) * mm});
            skLineSegment(sketch, "E221.1", {"start": v(12.67, 26) * mm, "end": v(6.96, 19.52) * mm});
            skLineSegment(sketch, "E221.2", {"start": v(6.96, 19.52) * mm, "end": v(12.27, 13.65) * mm});
            skLineSegment(sketch, "E221.3", {"start": v(17.98, 20.33) * mm, "end": v(12.27, 13.65) * mm});
            skLineSegment(sketch, "E222", {"start": v(18.26, 6.25) * mm, "end": v(12, -1.25) * mm, "construction": true});
            skLineSegment(sketch, "E223.0", {"start": v(6.7, 5.54) * mm, "end": v(12, -0.47) * mm});
            skLineSegment(sketch, "E223.1", {"start": v(12.3, 12.1) * mm, "end": v(6.7, 5.54) * mm});
            skLineSegment(sketch, "E223.2", {"start": v(12.3, 12.1) * mm, "end": v(17.6, 6.24) * mm});
            skLineSegment(sketch, "E223.3", {"start": v(17.6, 6.24) * mm, "end": v(12, -0.47) * mm});
            skLineSegment(sketch, "E224", {"start": v(18.53, -8.66) * mm, "end": v(25.05, -16.08) * mm, "construction": true});
            skLineSegment(sketch, "E225.0", {"start": v(12.02, -2.03) * mm, "end": v(17.86, -8.67) * mm});
            skLineSegment(sketch, "E225.1", {"start": v(12.02, -2.03) * mm, "end": v(6.63, -8.5) * mm});
            skLineSegment(sketch, "E225.2", {"start": v(6.63, -8.5) * mm, "end": v(12.39, -15.25) * mm});
            skLineSegment(sketch, "E225.3", {"start": v(17.86, -8.67) * mm, "end": v(12.39, -15.25) * mm});
            skLineSegment(sketch, "E226", {"start": v(18.82, -23.56) * mm, "end": v(25.24, -31.09) * mm, "construction": true});
            skLineSegment(sketch, "E227.0", {"start": v(12.4, -16.82) * mm, "end": v(18.15, -23.56) * mm});
            skLineSegment(sketch, "E227.1", {"start": v(12.4, -16.82) * mm, "end": v(7.01, -23.28) * mm});
            skLineSegment(sketch, "E227.2", {"start": v(7.01, -23.28) * mm, "end": v(12.7, -30.1) * mm});
            skLineSegment(sketch, "E227.3", {"start": v(18.15, -23.56) * mm, "end": v(12.7, -30.1) * mm});
            skLineSegment(sketch, "E228.0", {"start": v(12.7, -31.7) * mm, "end": v(18.39, -38.52) * mm});
            skLineSegment(sketch, "E228.1", {"start": v(12.7, -31.7) * mm, "end": v(7.01, -38.52) * mm});
            skLineSegment(sketch, "E228.2", {"start": v(7.01, -38.52) * mm, "end": v(12.7, -45.35) * mm});
            skLineSegment(sketch, "E228.3", {"start": v(18.39, -38.52) * mm, "end": v(12.7, -45.35) * mm});
            skLineSegment(sketch, "E229.0", {"start": v(6.35, -39.32) * mm, "end": v(11.62, -45.63) * mm});
            skLineSegment(sketch, "E229.1", {"start": v(6.35, -39.32) * mm, "end": v(1.08, -45.63) * mm});
            skLineSegment(sketch, "E229.2", {"start": v(11.62, -45.63) * mm, "end": v(1.08, -45.63) * mm});
            skLineSegment(sketch, "E230", {"start": v(-18.53, -8.66) * mm, "end": v(-12.4, -16.03) * mm, "construction": true});
            skLineSegment(sketch, "E231.0", {"start": v(-12.53, 25.86) * mm, "end": v(-17.88, 20.2) * mm});
            skLineSegment(sketch, "E231.1", {"start": v(-12.53, 25.86) * mm, "end": v(-6.73, 19.27) * mm});
            skLineSegment(sketch, "E231.2", {"start": v(-6.73, 19.27) * mm, "end": v(-12.1, 13.42) * mm});
            skLineSegment(sketch, "E231.3", {"start": v(-17.88, 20.2) * mm, "end": v(-12.1, 13.42) * mm});
            skLineSegment(sketch, "E232.0", {"start": v(-12.12, 11.9) * mm, "end": v(-17.46, 6.08) * mm});
            skLineSegment(sketch, "E232.1", {"start": v(-12.12, 11.9) * mm, "end": v(-6.7, 5.54) * mm});
            skLineSegment(sketch, "E232.2", {"start": v(-6.7, 5.54) * mm, "end": v(-12, -0.47) * mm});
            skLineSegment(sketch, "E232.3", {"start": v(-17.46, 6.08) * mm, "end": v(-12, -0.47) * mm});
            skLineSegment(sketch, "E233.0", {"start": v(-12.02, -2.03) * mm, "end": v(-17.86, -8.67) * mm});
            skLineSegment(sketch, "E233.1", {"start": v(-12.02, -2.03) * mm, "end": v(-6.63, -8.5) * mm});
            skLineSegment(sketch, "E233.2", {"start": v(-6.63, -8.5) * mm, "end": v(-12.39, -15.25) * mm});
            skLineSegment(sketch, "E233.3", {"start": v(-17.86, -8.67) * mm, "end": v(-12.39, -15.25) * mm});
            skLineSegment(sketch, "E234.0", {"start": v(-12.4, -16.82) * mm, "end": v(-18.15, -23.56) * mm});
            skLineSegment(sketch, "E234.1", {"start": v(-12.4, -16.82) * mm, "end": v(-7.01, -23.28) * mm});
            skLineSegment(sketch, "E234.2", {"start": v(-7.01, -23.28) * mm, "end": v(-12.7, -30.1) * mm});
            skLineSegment(sketch, "E234.3", {"start": v(-18.15, -23.56) * mm, "end": v(-12.7, -30.1) * mm});
            skLineSegment(sketch, "E235.0", {"start": v(-12.44, -38.52) * mm, "end": v(-12.7, -38.84) * mm});
            skLineSegment(sketch, "E235.1", {"start": v(-12.96, -38.52) * mm, "end": v(-12.7, -38.84) * mm});
            skLineSegment(sketch, "E235.3", {"start": v(-12.7, -38.2) * mm, "end": v(-12.44, -38.52) * mm});
            skLineSegment(sketch, "E236.0", {"start": v(-25.06, 27.04) * mm, "end": v(-30.46, 21.68) * mm});
            skLineSegment(sketch, "E236.1", {"start": v(-25.06, 27.04) * mm, "end": v(-19.25, 20.24) * mm});
            skLineSegment(sketch, "E236.2", {"start": v(-19.25, 20.24) * mm, "end": v(-24.57, 14.62) * mm});
            skLineSegment(sketch, "E236.3", {"start": v(-30.46, 21.68) * mm, "end": v(-24.57, 14.62) * mm});
            skLineSegment(sketch, "E237.0", {"start": v(-24.62, 13.09) * mm, "end": v(-18.8, 6.11) * mm});
            skLineSegment(sketch, "E237.1", {"start": v(-24.62, 13.09) * mm, "end": v(-30.67, 6.7) * mm});
            skLineSegment(sketch, "E237.2", {"start": v(-30.67, 6.7) * mm, "end": v(-24.77, -0.39) * mm});
            skLineSegment(sketch, "E237.3", {"start": v(-18.8, 6.11) * mm, "end": v(-24.77, -0.39) * mm});
            skLineSegment(sketch, "E238", {"start": v(-18.53, -8.66) * mm, "end": v(-25.05, -16.08) * mm, "construction": true});
            skLineSegment(sketch, "E239.0", {"start": v(-24.8, -1.93) * mm, "end": v(-19.2, -8.66) * mm});
            skLineSegment(sketch, "E239.1", {"start": v(-24.8, -1.93) * mm, "end": v(-30.77, -8.43) * mm});
            skLineSegment(sketch, "E239.2", {"start": v(-30.77, -8.43) * mm, "end": v(-25.04, -15.3) * mm});
            skLineSegment(sketch, "E239.3", {"start": v(-19.2, -8.66) * mm, "end": v(-25.04, -15.3) * mm});
            skLineSegment(sketch, "E240.0", {"start": v(-25.06, -16.86) * mm, "end": v(-19.48, -23.56) * mm});
            skLineSegment(sketch, "E240.1", {"start": v(-25.06, -16.86) * mm, "end": v(-30.9, -23.5) * mm});
            skLineSegment(sketch, "E240.2", {"start": v(-30.9, -23.5) * mm, "end": v(-25.24, -30.3) * mm});
            skLineSegment(sketch, "E240.3", {"start": v(-19.48, -23.56) * mm, "end": v(-25.24, -30.3) * mm});
            skLineSegment(sketch, "E241.0", {"start": v(-25.25, -31.88) * mm, "end": v(-19.71, -38.52) * mm});
            skLineSegment(sketch, "E241.1", {"start": v(-25.25, -31.88) * mm, "end": v(-31, -38.62) * mm});
            skLineSegment(sketch, "E241.2", {"start": v(-31, -38.62) * mm, "end": v(-25.4, -45.35) * mm});
            skLineSegment(sketch, "E241.3", {"start": v(-19.71, -38.52) * mm, "end": v(-25.4, -45.35) * mm});
            skLineSegment(sketch, "E242", {"start": v(18.67, 20.34) * mm, "end": v(24.67, 13.94) * mm, "construction": true});
            skLineSegment(sketch, "E243.0", {"start": v(25.09, 27.07) * mm, "end": v(30.48, 21.7) * mm});
            skLineSegment(sketch, "E243.1", {"start": v(25.09, 27.07) * mm, "end": v(19.36, 20.36) * mm});
            skLineSegment(sketch, "E243.2", {"start": v(19.36, 20.36) * mm, "end": v(24.64, 14.7) * mm});
            skLineSegment(sketch, "E243.3", {"start": v(30.48, 21.7) * mm, "end": v(24.64, 14.7) * mm});
            skLineSegment(sketch, "E244", {"start": v(18.26, 6.25) * mm, "end": v(24.88, -1.05) * mm, "construction": true});
            skLineSegment(sketch, "E245", {"start": v(18.26, 6.25) * mm, "end": v(24.67, 13.94) * mm, "construction": true});
            skLineSegment(sketch, "E246.0", {"start": v(18.94, 6.27) * mm, "end": v(24.69, 13.17) * mm});
            skLineSegment(sketch, "E246.1", {"start": v(18.94, 6.27) * mm, "end": v(24.86, -0.28) * mm});
            skLineSegment(sketch, "E246.2", {"start": v(30.7, 6.74) * mm, "end": v(24.86, -0.28) * mm});
            skLineSegment(sketch, "E246.3", {"start": v(24.69, 13.17) * mm, "end": v(30.7, 6.74) * mm});
            skLineSegment(sketch, "E247.0", {"start": v(24.9, -1.83) * mm, "end": v(19.2, -8.66) * mm});
            skLineSegment(sketch, "E247.1", {"start": v(24.9, -1.83) * mm, "end": v(30.81, -8.37) * mm});
            skLineSegment(sketch, "E247.2", {"start": v(30.81, -8.37) * mm, "end": v(25.04, -15.3) * mm});
            skLineSegment(sketch, "E247.3", {"start": v(19.2, -8.66) * mm, "end": v(25.04, -15.3) * mm});
            skLineSegment(sketch, "E248.0", {"start": v(25.06, -16.86) * mm, "end": v(19.48, -23.56) * mm});
            skLineSegment(sketch, "E248.1", {"start": v(25.06, -16.86) * mm, "end": v(30.9, -23.5) * mm});
            skLineSegment(sketch, "E248.2", {"start": v(30.9, -23.5) * mm, "end": v(25.24, -30.3) * mm});
            skLineSegment(sketch, "E248.3", {"start": v(19.48, -23.56) * mm, "end": v(25.24, -30.3) * mm});
            skLineSegment(sketch, "E249", {"start": v(19.05, -38.52) * mm, "end": v(25.4, -46.14) * mm, "construction": true});
            skLineSegment(sketch, "E250", {"start": v(19.05, -38.52) * mm, "end": v(25.24, -31.09) * mm, "construction": true});
            skLineSegment(sketch, "E251.0", {"start": v(19.71, -38.52) * mm, "end": v(25.25, -31.88) * mm});
            skLineSegment(sketch, "E251.1", {"start": v(19.71, -38.52) * mm, "end": v(25.4, -45.35) * mm});
            skLineSegment(sketch, "E251.2", {"start": v(31, -38.62) * mm, "end": v(25.4, -45.35) * mm});
            skLineSegment(sketch, "E251.3", {"start": v(25.25, -31.88) * mm, "end": v(31, -38.62) * mm});
            skLineSegment(sketch, "E252.0", {"start": v(-12.7, -31.7) * mm, "end": v(-18.39, -38.52) * mm});
            skLineSegment(sketch, "E252.1", {"start": v(-12.7, -31.7) * mm, "end": v(-7.01, -38.52) * mm});
            skLineSegment(sketch, "E252.2", {"start": v(-7.01, -38.52) * mm, "end": v(-12.7, -45.35) * mm});
            skLineSegment(sketch, "E252.3", {"start": v(-18.39, -38.52) * mm, "end": v(-12.7, -45.35) * mm});
            skLineSegment(sketch, "E253", {"start": v(19.05, -38.52) * mm, "end": v(12.7, -46.14) * mm, "construction": true});
            skLineSegment(sketch, "E254", {"start": v(18.94, 33.92) * mm, "end": v(18.67, 20.34) * mm, "construction": true});
            skLineSegment(sketch, "E255", {"start": v(18.67, 20.34) * mm, "end": v(18.26, 6.25) * mm, "construction": true});
            skLineSegment(sketch, "E256", {"start": v(18.26, 6.25) * mm, "end": v(18.53, -8.66) * mm, "construction": true});
            skLineSegment(sketch, "E257", {"start": v(18.53, -8.66) * mm, "end": v(18.82, -23.56) * mm, "construction": true});
            skLineSegment(sketch, "E258", {"start": v(18.82, -23.56) * mm, "end": v(19.05, -38.52) * mm, "construction": true});
            skLineSegment(sketch, "E259", {"start": v(19.05, -38.52) * mm, "end": v(19.08, -46.14) * mm, "construction": true});
            skLineSegment(sketch, "E260", {"start": v(-18.9, 33.86) * mm, "end": v(-18.57, 20.22) * mm, "construction": true});
            skLineSegment(sketch, "E261", {"start": v(-18.57, 20.22) * mm, "end": v(-18.13, 6.1) * mm, "construction": true});
            skLineSegment(sketch, "E262", {"start": v(-18.13, 6.1) * mm, "end": v(-18.53, -8.66) * mm, "construction": true});
            skLineSegment(sketch, "E263", {"start": v(-18.53, -8.66) * mm, "end": v(-18.82, -23.56) * mm, "construction": true});
            skLineSegment(sketch, "E264", {"start": v(-18.82, -23.56) * mm, "end": v(-19.05, -38.52) * mm, "construction": true});
            skLineSegment(sketch, "E265", {"start": v(-19.05, -38.52) * mm, "end": v(-19.02, -46.14) * mm, "construction": true});
            skLineSegment(sketch, "E266.0", {"start": v(19.43, 32.72) * mm, "end": v(19.2, 21.75) * mm});
            skLineSegment(sketch, "E266.1", {"start": v(19.43, 32.72) * mm, "end": v(24.37, 27.8) * mm});
            skLineSegment(sketch, "E266.2", {"start": v(24.37, 27.8) * mm, "end": v(19.2, 21.75) * mm});
            skLineSegment(sketch, "E267.0", {"start": v(18.4, 32.54) * mm, "end": v(18.2, 21.6) * mm});
            skLineSegment(sketch, "E267.1", {"start": v(18.4, 32.54) * mm, "end": v(13.34, 26.79) * mm});
            skLineSegment(sketch, "E267.2", {"start": v(13.34, 26.79) * mm, "end": v(18.2, 21.6) * mm});
            skLineSegment(sketch, "E268.0", {"start": v(19.15, 19.1) * mm, "end": v(18.81, 7.7) * mm});
            skLineSegment(sketch, "E268.1", {"start": v(19.15, 19.1) * mm, "end": v(23.99, 13.92) * mm});
            skLineSegment(sketch, "E268.2", {"start": v(18.81, 7.7) * mm, "end": v(23.99, 13.92) * mm});
            skLineSegment(sketch, "E269.0", {"start": v(18.12, 18.92) * mm, "end": v(17.8, 7.53) * mm});
            skLineSegment(sketch, "E269.1", {"start": v(18.12, 18.92) * mm, "end": v(12.96, 12.87) * mm});
            skLineSegment(sketch, "E269.2", {"start": v(12.96, 12.87) * mm, "end": v(17.8, 7.53) * mm});
            skLineSegment(sketch, "E270.0", {"start": v(17.78, 4.88) * mm, "end": v(12.68, -1.24) * mm});
            skLineSegment(sketch, "E270.1", {"start": v(17.78, 4.88) * mm, "end": v(18, -7.3) * mm});
            skLineSegment(sketch, "E270.2", {"start": v(12.68, -1.24) * mm, "end": v(18, -7.3) * mm});
            skLineSegment(sketch, "E271.0", {"start": v(18.8, 4.9) * mm, "end": v(19.01, -7.3) * mm});
            skLineSegment(sketch, "E271.1", {"start": v(18.8, 4.9) * mm, "end": v(24.2, -1.07) * mm});
            skLineSegment(sketch, "E271.2", {"start": v(24.2, -1.07) * mm, "end": v(19.01, -7.3) * mm});
            skLineSegment(sketch, "E272.0", {"start": v(18.05, -10.04) * mm, "end": v(13.05, -16.03) * mm});
            skLineSegment(sketch, "E272.1", {"start": v(18.05, -10.04) * mm, "end": v(18.28, -22.15) * mm});
            skLineSegment(sketch, "E272.2", {"start": v(13.05, -16.03) * mm, "end": v(18.28, -22.15) * mm});
            skLineSegment(sketch, "E273.0", {"start": v(19.07, -10.04) * mm, "end": v(19.3, -22.19) * mm});
            skLineSegment(sketch, "E273.1", {"start": v(19.07, -10.04) * mm, "end": v(24.39, -16.09) * mm});
            skLineSegment(sketch, "E273.2", {"start": v(24.39, -16.09) * mm, "end": v(19.3, -22.19) * mm});
            skLineSegment(sketch, "E274.0", {"start": v(18.34, -24.92) * mm, "end": v(18.53, -37.11) * mm});
            skLineSegment(sketch, "E274.1", {"start": v(18.34, -24.92) * mm, "end": v(13.35, -30.9) * mm});
            skLineSegment(sketch, "E274.2", {"start": v(13.35, -30.9) * mm, "end": v(18.53, -37.11) * mm});
            skLineSegment(sketch, "E275.0", {"start": v(19.36, -24.98) * mm, "end": v(19.54, -37.12) * mm});
            skLineSegment(sketch, "E275.1", {"start": v(19.36, -24.98) * mm, "end": v(24.57, -31.1) * mm});
            skLineSegment(sketch, "E275.2", {"start": v(19.54, -37.12) * mm, "end": v(24.57, -31.1) * mm});
            skLineSegment(sketch, "E276.0", {"start": v(18.55, -39.9) * mm, "end": v(18.57, -45.64) * mm});
            skLineSegment(sketch, "E276.1", {"start": v(18.55, -39.9) * mm, "end": v(13.77, -45.64) * mm});
            skLineSegment(sketch, "E276.2", {"start": v(18.57, -45.64) * mm, "end": v(13.77, -45.64) * mm});
            skLineSegment(sketch, "E277.0", {"start": v(19.56, -39.92) * mm, "end": v(19.58, -45.64) * mm});
            skLineSegment(sketch, "E277.1", {"start": v(19.56, -39.92) * mm, "end": v(24.33, -45.64) * mm});
            skLineSegment(sketch, "E277.2", {"start": v(24.33, -45.64) * mm, "end": v(19.58, -45.64) * mm});
            skLineSegment(sketch, "E278.0", {"start": v(-19.38, 32.65) * mm, "end": v(-19.12, 21.67) * mm});
            skLineSegment(sketch, "E278.1", {"start": v(-19.38, 32.65) * mm, "end": v(-24.32, 27.75) * mm});
            skLineSegment(sketch, "E278.2", {"start": v(-24.32, 27.75) * mm, "end": v(-19.12, 21.67) * mm});
            skLineSegment(sketch, "E279.0", {"start": v(-18.35, 32.48) * mm, "end": v(-18.09, 21.47) * mm});
            skLineSegment(sketch, "E279.1", {"start": v(-18.35, 32.48) * mm, "end": v(-13.2, 26.63) * mm});
            skLineSegment(sketch, "E279.2", {"start": v(-13.2, 26.63) * mm, "end": v(-18.09, 21.47) * mm});
            skLineSegment(sketch, "E280.0", {"start": v(-19.03, 19) * mm, "end": v(-23.92, 13.83) * mm});
            skLineSegment(sketch, "E280.1", {"start": v(-19.03, 19) * mm, "end": v(-18.68, 7.54) * mm});
            skLineSegment(sketch, "E280.2", {"start": v(-23.92, 13.83) * mm, "end": v(-18.68, 7.54) * mm});
            skLineSegment(sketch, "E281.0", {"start": v(-18.01, 18.78) * mm, "end": v(-17.66, 7.37) * mm});
            skLineSegment(sketch, "E281.1", {"start": v(-18.01, 18.78) * mm, "end": v(-12.8, 12.67) * mm});
            skLineSegment(sketch, "E281.2", {"start": v(-12.8, 12.67) * mm, "end": v(-17.66, 7.37) * mm});
            skLineSegment(sketch, "E282.0", {"start": v(-18.67, 4.78) * mm, "end": v(-19, -7.33) * mm});
            skLineSegment(sketch, "E282.1", {"start": v(-18.67, 4.78) * mm, "end": v(-24.13, -1.17) * mm});
            skLineSegment(sketch, "E282.2", {"start": v(-24.13, -1.17) * mm, "end": v(-19, -7.33) * mm});
            skLineSegment(sketch, "E283.0", {"start": v(-17.66, 4.74) * mm, "end": v(-17.99, -7.28) * mm});
            skLineSegment(sketch, "E283.1", {"start": v(-17.66, 4.74) * mm, "end": v(-12.68, -1.24) * mm});
            skLineSegment(sketch, "E283.2", {"start": v(-12.68, -1.24) * mm, "end": v(-17.99, -7.28) * mm});
            skLineSegment(sketch, "E284.0", {"start": v(-19.06, -10.01) * mm, "end": v(-24.4, -16.09) * mm});
            skLineSegment(sketch, "E284.1", {"start": v(-19.06, -10.01) * mm, "end": v(-19.29, -22.22) * mm});
            skLineSegment(sketch, "E284.2", {"start": v(-24.4, -16.09) * mm, "end": v(-19.29, -22.22) * mm});
            skLineSegment(sketch, "E285.0", {"start": v(-19.35, -24.96) * mm, "end": v(-24.58, -31.1) * mm});
            skLineSegment(sketch, "E285.1", {"start": v(-19.35, -24.96) * mm, "end": v(-19.54, -37.14) * mm});
            skLineSegment(sketch, "E285.2", {"start": v(-24.58, -31.1) * mm, "end": v(-19.54, -37.14) * mm});
            skLineSegment(sketch, "E286.0", {"start": v(-18.33, -24.94) * mm, "end": v(-18.52, -37.1) * mm});
            skLineSegment(sketch, "E286.1", {"start": v(-18.33, -24.94) * mm, "end": v(-13.36, -30.9) * mm});
            skLineSegment(sketch, "E286.2", {"start": v(-13.36, -30.9) * mm, "end": v(-18.52, -37.1) * mm});
            skLineSegment(sketch, "E287.0", {"start": v(-19.55, -39.92) * mm, "end": v(-24.32, -45.63) * mm});
            skLineSegment(sketch, "E287.1", {"start": v(-19.55, -39.92) * mm, "end": v(-19.53, -45.63) * mm});
            skLineSegment(sketch, "E287.2", {"start": v(-19.53, -45.63) * mm, "end": v(-24.32, -45.63) * mm});
            skLineSegment(sketch, "E288.0", {"start": v(-18.54, -39.92) * mm, "end": v(-18.52, -45.64) * mm});
            skLineSegment(sketch, "E288.1", {"start": v(-18.54, -39.92) * mm, "end": v(-13.78, -45.64) * mm});
            skLineSegment(sketch, "E288.2", {"start": v(-13.78, -45.64) * mm, "end": v(-18.52, -45.64) * mm});
            skLineSegment(sketch, "E289.0", {"start": v(-18.06, -10.02) * mm, "end": v(-13.04, -16.03) * mm});
            skLineSegment(sketch, "E289.1", {"start": v(-18.06, -10.02) * mm, "end": v(-18.3, -22.17) * mm});
            skLineSegment(sketch, "E289.2", {"start": v(-13.04, -16.03) * mm, "end": v(-18.3, -22.17) * mm});
            skLineSegment(sketch, "E290", {"start": v(-38.1, 30.06) * mm, "end": v(-19.02, 46.83) * mm});
            skLineSegment(sketch, "E291", {"start": v(-38.1, 30.06) * mm, "end": v(-38.1, 72.44) * mm});
            skLineSegment(sketch, "E292", {"start": v(38.1, 30.06) * mm, "end": v(38.1, 74.77) * mm});
            skLineSegment(sketch, "E293", {"start": v(38.1, 74.77) * mm, "end": v(-37.89, 74.77) * mm});
            skLineSegment(sketch, "E294", {"start": v(-37.89, 74.77) * mm, "end": v(-38.1, 72.44) * mm});
            skLineSegment(sketch, "E295", {"start": v(-19.02, 46.83) * mm, "end": v(-12.48, 40.22) * mm});
            skLineSegment(sketch, "E296", {"start": v(-12.48, 40.22) * mm, "end": v(12.92, 39.93) * mm});
            skLineSegment(sketch, "E297", {"start": v(12.92, 39.93) * mm, "end": v(19.08, 46.9) * mm});
            skLineSegment(sketch, "E298", {"start": v(19.08, 46.9) * mm, "end": v(38.1, 30.06) * mm});
            skPoint(sketch, "E299", {"position": v(0, -1.52) * mm});
            skSolve(sketch);
        }
        {
            var Q0;
            {var subQ0=sQuery(id+"F0.wireOp",EDGE,"E9");Q0=makeQuery(id+"F0.imprint","IMPRINT",FACE,{"disambiguationData":[TD([[makeQuery(id+"F0.imprint","IMPRINT",EDGE,{"derivedFrom":subQ0}),1.0]])]});}
            var Q1;
            {var subQ3=sQuery(id+"F0.wireOp",EDGE,"E9");Q1=makeQuery(id+"F0.imprint","IMPRINT",FACE,{"disambiguationData":[TD([[makeQuery(id+"F0.imprint","IMPRINT",EDGE,{"derivedFrom":subQ3}),-1.0]])]});}
            var Q2;
            {var subQ0=sQuery(id+"F0.wireOp",EDGE,"E5");var subQ1=sQuery(id+"F0.wireOp",EDGE,"E1");var subQ2=makeQuery(id+"F0.imprint","INTERSECT",VERTEX,{"derivedFrom":[subQ1,subQ0]});Q2=makeQuery(id+"F0.imprint","IMPRINT",FACE,{"disambiguationData":[TD([[makeQuery(id+"F0.imprint","IMPRINT",EDGE,{"disambiguationData":[TD([[subQ2,-1.0]])],"derivedFrom":subQ0}),-1.0]])]});}
            var Q3;
            {var subQ0=sQuery(id+"F0.wireOp",EDGE,"E3");var subQ1=sQuery(id+"F0.wireOp",EDGE,"E1");var subQ2=makeQuery(id+"F0.imprint","INTERSECT",VERTEX,{"derivedFrom":[subQ1,subQ0]});Q3=makeQuery(id+"F0.imprint","IMPRINT",FACE,{"disambiguationData":[TD([[makeQuery(id+"F0.imprint","IMPRINT",EDGE,{"disambiguationData":[TD([[subQ2,-1.0]])],"derivedFrom":subQ1}),-1.0]])]});}
            extrude(context, id + "F2", {"entities" : qUnion([Q0, Q1, Q2, Q3]), "endBound" : BoundingType.SYMMETRIC, "depth" : 93.22 * mm, "offsetDistance" : 25.4 * mm});
        }
        {
            var Q0;
            Q0=makeQuery(id+"F1.imprint","IMPRINT",FACE,{"disambiguationData":[TD([[makeQuery(id+"F1.imprint","IMPRINT",EDGE,{"derivedFrom":sQuery(id+"F1.wireOp",EDGE,"E273.0")}),1.0]])]});
            var Q1;
            Q1=makeQuery(id+"F1.imprint","IMPRINT",FACE,{"disambiguationData":[TD([[makeQuery(id+"F1.imprint","IMPRINT",EDGE,{"derivedFrom":sQuery(id+"F1.wireOp",EDGE,"E239.0")}),-1.0]])]});
            var Q2;
            Q2=makeQuery(id+"F1.imprint","IMPRINT",FACE,{"disambiguationData":[TD([[makeQuery(id+"F1.imprint","IMPRINT",EDGE,{"derivedFrom":sQuery(id+"F1.wireOp",EDGE,"E168.0")}),1.0]])]});
            var Q3;
            Q3=makeQuery(id+"F1.imprint","IMPRINT",FACE,{"disambiguationData":[TD([[makeQuery(id+"F1.imprint","IMPRINT",EDGE,{"derivedFrom":sQuery(id+"F1.wireOp",EDGE,"E220.0")}),-1.0]])]});
            var Q4;
            Q4=makeQuery(id+"F1.imprint","IMPRINT",FACE,{"disambiguationData":[TD([[makeQuery(id+"F1.imprint","IMPRINT",EDGE,{"derivedFrom":sQuery(id+"F1.wireOp",EDGE,"E218.0")}),-1.0]])]});
            var Q5;
            Q5=makeQuery(id+"F1.imprint","IMPRINT",FACE,{"disambiguationData":[TD([[makeQuery(id+"F1.imprint","IMPRINT",EDGE,{"derivedFrom":sQuery(id+"F1.wireOp",EDGE,"E73.0")}),1.0]])]});
            var Q6;
            Q6=makeQuery(id+"F1.imprint","IMPRINT",FACE,{"disambiguationData":[TD([[makeQuery(id+"F1.imprint","IMPRINT",EDGE,{"derivedFrom":sQuery(id+"F1.wireOp",EDGE,"E272.0")}),1.0]])]});
            var Q7;
            Q7=makeQuery(id+"F1.imprint","IMPRINT",FACE,{"disambiguationData":[TD([[makeQuery(id+"F1.imprint","IMPRINT",EDGE,{"derivedFrom":sQuery(id+"F1.wireOp",EDGE,"E282.0")}),-1.0]])]});
            var Q8;
            Q8=makeQuery(id+"F1.imprint","IMPRINT",FACE,{"disambiguationData":[TD([[makeQuery(id+"F1.imprint","IMPRINT",EDGE,{"derivedFrom":sQuery(id+"F1.wireOp",EDGE,"E240.0")}),-1.0]])]});
            var Q9;
            Q9=makeQuery(id+"F1.imprint","IMPRINT",FACE,{"disambiguationData":[TD([[makeQuery(id+"F1.imprint","IMPRINT",EDGE,{"derivedFrom":sQuery(id+"F1.wireOp",EDGE,"E172.0")}),1.0]])]});
            var Q10;
            Q10=makeQuery(id+"F1.imprint","IMPRINT",FACE,{"disambiguationData":[TD([[makeQuery(id+"F1.imprint","IMPRINT",EDGE,{"derivedFrom":sQuery(id+"F1.wireOp",EDGE,"E278.0")}),-1.0]])]});
            var Q11;
            Q11=makeQuery(id+"F1.imprint","IMPRINT",FACE,{"disambiguationData":[TD([[makeQuery(id+"F1.imprint","IMPRINT",EDGE,{"derivedFrom":sQuery(id+"F1.wireOp",EDGE,"E147.0")}),-1.0]])]});
            var Q12;
            Q12=makeQuery(id+"F1.imprint","IMPRINT",FACE,{"disambiguationData":[TD([[makeQuery(id+"F1.imprint","IMPRINT",EDGE,{"derivedFrom":sQuery(id+"F1.wireOp",EDGE,"E100.0")}),-1.0]])]});
            var Q13;
            Q13=makeQuery(id+"F1.imprint","IMPRINT",FACE,{"disambiguationData":[TD([[makeQuery(id+"F1.imprint","IMPRINT",EDGE,{"derivedFrom":sQuery(id+"F1.wireOp",EDGE,"E289.0")}),-1.0]])]});
            var Q14;
            Q14=makeQuery(id+"F1.imprint","IMPRINT",FACE,{"disambiguationData":[TD([[makeQuery(id+"F1.imprint","IMPRINT",EDGE,{"derivedFrom":sQuery(id+"F1.wireOp",EDGE,"E266.0")}),1.0]])]});
            var Q15;
            Q15=makeQuery(id+"F1.imprint","IMPRINT",FACE,{"disambiguationData":[TD([[makeQuery(id+"F1.imprint","IMPRINT",EDGE,{"derivedFrom":sQuery(id+"F1.wireOp",EDGE,"E281.0")}),1.0]])]});
            var Q16;
            Q16=makeQuery(id+"F1.imprint","IMPRINT",FACE,{"disambiguationData":[TD([[makeQuery(id+"F1.imprint","IMPRINT",EDGE,{"derivedFrom":sQuery(id+"F1.wireOp",EDGE,"E114.0")}),-1.0]])]});
            var Q17;
            Q17=makeQuery(id+"F1.imprint","IMPRINT",FACE,{"disambiguationData":[TD([[makeQuery(id+"F1.imprint","IMPRINT",EDGE,{"derivedFrom":sQuery(id+"F1.wireOp",EDGE,"E270.0")}),1.0]])]});
            var Q18;
            Q18=makeQuery(id+"F1.imprint","IMPRINT",FACE,{"disambiguationData":[TD([[makeQuery(id+"F1.imprint","IMPRINT",EDGE,{"derivedFrom":sQuery(id+"F1.wireOp",EDGE,"E140.0")}),-1.0]])]});
            var Q19;
            Q19=makeQuery(id+"F1.imprint","IMPRINT",FACE,{"disambiguationData":[TD([[makeQuery(id+"F1.imprint","IMPRINT",EDGE,{"derivedFrom":sQuery(id+"F1.wireOp",EDGE,"E167.0")}),1.0]])]});
            var Q20;
            Q20=makeQuery(id+"F1.imprint","IMPRINT",FACE,{"disambiguationData":[TD([[makeQuery(id+"F1.imprint","IMPRINT",EDGE,{"derivedFrom":sQuery(id+"F1.wireOp",EDGE,"E228.0")}),-1.0]])]});
            var Q21;
            Q21=makeQuery(id+"F1.imprint","IMPRINT",FACE,{"disambiguationData":[TD([[makeQuery(id+"F1.imprint","IMPRINT",EDGE,{"derivedFrom":sQuery(id+"F1.wireOp",EDGE,"E113.0")}),-1.0]])]});
            var Q22;
            Q22=makeQuery(id+"F1.imprint","IMPRINT",FACE,{"disambiguationData":[TD([[makeQuery(id+"F1.imprint","IMPRINT",EDGE,{"derivedFrom":sQuery(id+"F1.wireOp",EDGE,"E139.0")}),-1.0]])]});
            var Q23;
            Q23=makeQuery(id+"F1.imprint","IMPRINT",FACE,{"disambiguationData":[TD([[makeQuery(id+"F1.imprint","IMPRINT",EDGE,{"derivedFrom":sQuery(id+"F1.wireOp",EDGE,"E181.0")}),1.0]])]});
            var Q24;
            Q24=makeQuery(id+"F1.imprint","IMPRINT",FACE,{"disambiguationData":[TD([[makeQuery(id+"F1.imprint","IMPRINT",EDGE,{"derivedFrom":sQuery(id+"F1.wireOp",EDGE,"E277.0")}),1.0]])]});
            var Q25;
            Q25=makeQuery(id+"F1.imprint","IMPRINT",FACE,{"disambiguationData":[TD([[makeQuery(id+"F1.imprint","IMPRINT",EDGE,{"derivedFrom":sQuery(id+"F1.wireOp",EDGE,"E143.0")}),1.0]])]});
            var Q26;
            Q26=makeQuery(id+"F1.imprint","IMPRINT",FACE,{"disambiguationData":[TD([[makeQuery(id+"F1.imprint","IMPRINT",EDGE,{"derivedFrom":sQuery(id+"F1.wireOp",EDGE,"E208.0")}),-1.0]])]});
            var Q27;
            Q27=makeQuery(id+"F1.imprint","IMPRINT",FACE,{"disambiguationData":[TD([[makeQuery(id+"F1.imprint","IMPRINT",EDGE,{"derivedFrom":sQuery(id+"F1.wireOp",EDGE,"E207.0")}),-1.0]])]});
            var Q28;
            Q28=makeQuery(id+"F1.imprint","IMPRINT",FACE,{"disambiguationData":[TD([[makeQuery(id+"F1.imprint","IMPRINT",EDGE,{"derivedFrom":sQuery(id+"F1.wireOp",EDGE,"E268.0")}),1.0]])]});
            var Q29;
            Q29=makeQuery(id+"F1.imprint","IMPRINT",FACE,{"disambiguationData":[TD([[makeQuery(id+"F1.imprint","IMPRINT",EDGE,{"derivedFrom":sQuery(id+"F1.wireOp",EDGE,"E232.0")}),1.0]])]});
            var Q30;
            Q30=makeQuery(id+"F1.imprint","IMPRINT",FACE,{"disambiguationData":[TD([[makeQuery(id+"F1.imprint","IMPRINT",EDGE,{"derivedFrom":sQuery(id+"F1.wireOp",EDGE,"E283.0")}),1.0]])]});
            var Q31;
            Q31=makeQuery(id+"F1.imprint","IMPRINT",FACE,{"disambiguationData":[TD([[makeQuery(id+"F1.imprint","IMPRINT",EDGE,{"derivedFrom":sQuery(id+"F1.wireOp",EDGE,"E223.0")}),1.0]])]});
            var Q32;
            Q32=makeQuery(id+"F1.imprint","IMPRINT",FACE,{"disambiguationData":[TD([[makeQuery(id+"F1.imprint","IMPRINT",EDGE,{"derivedFrom":sQuery(id+"F1.wireOp",EDGE,"E158.0")}),-1.0]])]});
            var Q33;
            Q33=makeQuery(id+"F1.imprint","IMPRINT",FACE,{"disambiguationData":[TD([[makeQuery(id+"F1.imprint","IMPRINT",EDGE,{"derivedFrom":sQuery(id+"F1.wireOp",EDGE,"E236.0")}),1.0]])]});
            var Q34;
            Q34=makeQuery(id+"F1.imprint","IMPRINT",FACE,{"disambiguationData":[TD([[makeQuery(id+"F1.imprint","IMPRINT",EDGE,{"derivedFrom":sQuery(id+"F1.wireOp",EDGE,"E274.0")}),-1.0]])]});
            var Q35;
            Q35=makeQuery(id+"F1.imprint","IMPRINT",FACE,{"disambiguationData":[TD([[makeQuery(id+"F1.imprint","IMPRINT",EDGE,{"derivedFrom":sQuery(id+"F1.wireOp",EDGE,"E117.0")}),-1.0]])]});
            var Q36;
            Q36=makeQuery(id+"F1.imprint","IMPRINT",FACE,{"disambiguationData":[TD([[makeQuery(id+"F1.imprint","IMPRINT",EDGE,{"derivedFrom":sQuery(id+"F1.wireOp",EDGE,"E231.0")}),1.0]])]});
            var Q37;
            Q37=makeQuery(id+"F1.imprint","IMPRINT",FACE,{"disambiguationData":[TD([[makeQuery(id+"F1.imprint","IMPRINT",EDGE,{"derivedFrom":sQuery(id+"F1.wireOp",EDGE,"E115.0")}),-1.0]])]});
            var Q38;
            Q38=makeQuery(id+"F1.imprint","IMPRINT",FACE,{"disambiguationData":[TD([[makeQuery(id+"F1.imprint","IMPRINT",EDGE,{"derivedFrom":sQuery(id+"F1.wireOp",EDGE,"E227.0")}),-1.0]])]});
            var Q39;
            Q39=makeQuery(id+"F1.imprint","IMPRINT",FACE,{"disambiguationData":[TD([[makeQuery(id+"F1.imprint","IMPRINT",EDGE,{"derivedFrom":sQuery(id+"F1.wireOp",EDGE,"E190.0")}),1.0]])]});
            var Q40;
            Q40=makeQuery(id+"F1.imprint","IMPRINT",FACE,{"disambiguationData":[TD([[makeQuery(id+"F1.imprint","IMPRINT",EDGE,{"derivedFrom":sQuery(id+"F1.wireOp",EDGE,"E271.0")}),1.0]])]});
            var Q41;
            Q41=makeQuery(id+"F1.imprint","IMPRINT",FACE,{"disambiguationData":[TD([[makeQuery(id+"F1.imprint","IMPRINT",EDGE,{"derivedFrom":sQuery(id+"F1.wireOp",EDGE,"E286.0")}),1.0]])]});
            var Q42;
            Q42=makeQuery(id+"F1.imprint","IMPRINT",FACE,{"disambiguationData":[TD([[makeQuery(id+"F1.imprint","IMPRINT",EDGE,{"derivedFrom":sQuery(id+"F1.wireOp",EDGE,"E205.0")}),-1.0]])]});
            var Q43;
            Q43=makeQuery(id+"F1.imprint","IMPRINT",FACE,{"disambiguationData":[TD([[makeQuery(id+"F1.imprint","IMPRINT",EDGE,{"derivedFrom":sQuery(id+"F1.wireOp",EDGE,"E276.0")}),-1.0]])]});
            var Q44;
            Q44=makeQuery(id+"F1.imprint","IMPRINT",FACE,{"disambiguationData":[TD([[makeQuery(id+"F1.imprint","IMPRINT",EDGE,{"derivedFrom":sQuery(id+"F1.wireOp",EDGE,"E287.0")}),1.0]])]});
            var Q45;
            Q45=makeQuery(id+"F1.imprint","IMPRINT",FACE,{"disambiguationData":[TD([[makeQuery(id+"F1.imprint","IMPRINT",EDGE,{"derivedFrom":sQuery(id+"F1.wireOp",EDGE,"E269.0")}),-1.0]])]});
            var Q46;
            Q46=makeQuery(id+"F1.imprint","IMPRINT",FACE,{"disambiguationData":[TD([[makeQuery(id+"F1.imprint","IMPRINT",EDGE,{"derivedFrom":sQuery(id+"F1.wireOp",EDGE,"E221.0")}),-1.0]])]});
            var Q47;
            Q47=makeQuery(id+"F1.imprint","IMPRINT",FACE,{"disambiguationData":[TD([[makeQuery(id+"F1.imprint","IMPRINT",EDGE,{"derivedFrom":sQuery(id+"F1.wireOp",EDGE,"E288.0")}),1.0]])]});
            var Q48;
            Q48=makeQuery(id+"F1.imprint","IMPRINT",FACE,{"disambiguationData":[TD([[makeQuery(id+"F1.imprint","IMPRINT",EDGE,{"derivedFrom":sQuery(id+"F1.wireOp",EDGE,"E195.0")}),1.0]])]});
            var Q49;
            Q49=makeQuery(id+"F1.imprint","IMPRINT",FACE,{"disambiguationData":[TD([[makeQuery(id+"F1.imprint","IMPRINT",EDGE,{"derivedFrom":sQuery(id+"F1.wireOp",EDGE,"E229.0")}),-1.0]])]});
            var Q50;
            Q50=makeQuery(id+"F1.imprint","IMPRINT",FACE,{"disambiguationData":[TD([[makeQuery(id+"F1.imprint","IMPRINT",EDGE,{"derivedFrom":sQuery(id+"F1.wireOp",EDGE,"E116.0")}),-1.0]])]});
            var Q51;
            Q51=makeQuery(id+"F1.imprint","IMPRINT",FACE,{"disambiguationData":[TD([[makeQuery(id+"F1.imprint","IMPRINT",EDGE,{"derivedFrom":sQuery(id+"F1.wireOp",EDGE,"E127.0")}),1.0]])]});
            var Q52;
            Q52=makeQuery(id+"F1.imprint","IMPRINT",FACE,{"disambiguationData":[TD([[makeQuery(id+"F1.imprint","IMPRINT",EDGE,{"derivedFrom":sQuery(id+"F1.wireOp",EDGE,"E237.0")}),-1.0]])]});
            var Q53;
            Q53=makeQuery(id+"F1.imprint","IMPRINT",FACE,{"disambiguationData":[TD([[makeQuery(id+"F1.imprint","IMPRINT",EDGE,{"derivedFrom":sQuery(id+"F1.wireOp",EDGE,"E247.0")}),1.0]])]});
            var Q54;
            Q54=makeQuery(id+"F1.imprint","IMPRINT",FACE,{"disambiguationData":[TD([[makeQuery(id+"F1.imprint","IMPRINT",EDGE,{"derivedFrom":sQuery(id+"F1.wireOp",EDGE,"E241.0")}),-1.0]])]});
            var Q55;
            Q55=makeQuery(id+"F1.imprint","IMPRINT",FACE,{"disambiguationData":[TD([[makeQuery(id+"F1.imprint","IMPRINT",EDGE,{"derivedFrom":sQuery(id+"F1.wireOp",EDGE,"E185.0")}),1.0]])]});
            var Q56;
            Q56=makeQuery(id+"F1.imprint","IMPRINT",FACE,{"disambiguationData":[TD([[makeQuery(id+"F1.imprint","IMPRINT",EDGE,{"derivedFrom":sQuery(id+"F1.wireOp",EDGE,"E211.0")}),1.0]])]});
            var Q57;
            Q57=makeQuery(id+"F1.imprint","IMPRINT",FACE,{"disambiguationData":[TD([[makeQuery(id+"F1.imprint","IMPRINT",EDGE,{"derivedFrom":sQuery(id+"F1.wireOp",EDGE,"E128.0")}),1.0]])]});
            var Q58;
            Q58=makeQuery(id+"F1.imprint","IMPRINT",FACE,{"disambiguationData":[TD([[makeQuery(id+"F1.imprint","IMPRINT",EDGE,{"derivedFrom":sQuery(id+"F1.wireOp",EDGE,"E93.0")}),-1.0]])]});
            var Q59;
            Q59=makeQuery(id+"F1.imprint","IMPRINT",FACE,{"disambiguationData":[TD([[makeQuery(id+"F1.imprint","IMPRINT",EDGE,{"derivedFrom":sQuery(id+"F1.wireOp",EDGE,"E285.0")}),1.0]])]});
            var Q60;
            Q60=makeQuery(id+"F1.imprint","IMPRINT",FACE,{"disambiguationData":[TD([[makeQuery(id+"F1.imprint","IMPRINT",EDGE,{"derivedFrom":sQuery(id+"F1.wireOp",EDGE,"E94.0")}),-1.0]])]});
            var Q61;
            Q61=makeQuery(id+"F1.imprint","IMPRINT",FACE,{"disambiguationData":[TD([[makeQuery(id+"F1.imprint","IMPRINT",EDGE,{"derivedFrom":sQuery(id+"F1.wireOp",EDGE,"E169.0")}),1.0]])]});
            var Q62;
            Q62=makeQuery(id+"F1.imprint","IMPRINT",FACE,{"disambiguationData":[TD([[makeQuery(id+"F1.imprint","IMPRINT",EDGE,{"derivedFrom":sQuery(id+"F1.wireOp",EDGE,"E112.0")}),-1.0]])]});
            var Q63;
            Q63=makeQuery(id+"F1.imprint","IMPRINT",FACE,{"disambiguationData":[TD([[makeQuery(id+"F1.imprint","IMPRINT",EDGE,{"derivedFrom":sQuery(id+"F1.wireOp",EDGE,"E146.0")}),1.0]])]});
            var Q64;
            Q64=makeQuery(id+"F1.imprint","IMPRINT",FACE,{"disambiguationData":[TD([[makeQuery(id+"F1.imprint","IMPRINT",EDGE,{"derivedFrom":sQuery(id+"F1.wireOp",EDGE,"E251.0")}),-1.0]])]});
            var Q65;
            Q65=makeQuery(id+"F1.imprint","IMPRINT",FACE,{"disambiguationData":[TD([[makeQuery(id+"F1.imprint","IMPRINT",EDGE,{"derivedFrom":sQuery(id+"F1.wireOp",EDGE,"E155.0")}),-1.0]])]});
            var Q66;
            Q66=makeQuery(id+"F1.imprint","IMPRINT",FACE,{"disambiguationData":[TD([[makeQuery(id+"F1.imprint","IMPRINT",EDGE,{"derivedFrom":sQuery(id+"F1.wireOp",EDGE,"E243.0")}),-1.0]])]});
            var Q67;
            Q67=makeQuery(id+"F1.imprint","IMPRINT",FACE,{"disambiguationData":[TD([[makeQuery(id+"F1.imprint","IMPRINT",EDGE,{"derivedFrom":sQuery(id+"F1.wireOp",EDGE,"E130.0")}),1.0]])]});
            var Q68;
            Q68=makeQuery(id+"F1.imprint","IMPRINT",FACE,{"disambiguationData":[TD([[makeQuery(id+"F1.imprint","IMPRINT",EDGE,{"derivedFrom":sQuery(id+"F1.wireOp",EDGE,"E74.0")}),1.0]])]});
            var Q69;
            Q69=makeQuery(id+"F1.imprint","IMPRINT",FACE,{"disambiguationData":[TD([[makeQuery(id+"F1.imprint","IMPRINT",EDGE,{"derivedFrom":sQuery(id+"F1.wireOp",EDGE,"E284.0")}),1.0]])]});
            var Q70;
            Q70=makeQuery(id+"F1.imprint","IMPRINT",FACE,{"disambiguationData":[TD([[makeQuery(id+"F1.imprint","IMPRINT",EDGE,{"derivedFrom":sQuery(id+"F1.wireOp",EDGE,"E141.0")}),-1.0]])]});
            var Q71;
            Q71=makeQuery(id+"F1.imprint","IMPRINT",FACE,{"disambiguationData":[TD([[makeQuery(id+"F1.imprint","IMPRINT",EDGE,{"derivedFrom":sQuery(id+"F1.wireOp",EDGE,"E219.0")}),1.0]])]});
            var Q72;
            Q72=makeQuery(id+"F1.imprint","IMPRINT",FACE,{"disambiguationData":[TD([[makeQuery(id+"F1.imprint","IMPRINT",EDGE,{"derivedFrom":sQuery(id+"F1.wireOp",EDGE,"E252.0")}),1.0]])]});
            var Q73;
            Q73=makeQuery(id+"F1.imprint","IMPRINT",FACE,{"disambiguationData":[TD([[makeQuery(id+"F1.imprint","IMPRINT",EDGE,{"derivedFrom":sQuery(id+"F1.wireOp",EDGE,"E157.0")}),-1.0]])]});
            var Q74;
            Q74=makeQuery(id+"F1.imprint","IMPRINT",FACE,{"disambiguationData":[TD([[makeQuery(id+"F1.imprint","IMPRINT",EDGE,{"derivedFrom":sQuery(id+"F1.wireOp",EDGE,"E142.0")}),-1.0]])]});
            var Q75;
            Q75=makeQuery(id+"F1.imprint","IMPRINT",FACE,{"disambiguationData":[TD([[makeQuery(id+"F1.imprint","IMPRINT",EDGE,{"derivedFrom":sQuery(id+"F1.wireOp",EDGE,"E246.0")}),-1.0]])]});
            var Q76;
            Q76=makeQuery(id+"F1.imprint","IMPRINT",FACE,{"disambiguationData":[TD([[makeQuery(id+"F1.imprint","IMPRINT",EDGE,{"derivedFrom":sQuery(id+"F1.wireOp",EDGE,"E280.0")}),1.0]])]});
            var Q77;
            Q77=makeQuery(id+"F1.imprint","IMPRINT",FACE,{"disambiguationData":[TD([[makeQuery(id+"F1.imprint","IMPRINT",EDGE,{"derivedFrom":sQuery(id+"F1.wireOp",EDGE,"E267.0")}),-1.0]])]});
            var Q78;
            Q78=makeQuery(id+"F1.imprint","IMPRINT",FACE,{"disambiguationData":[TD([[makeQuery(id+"F1.imprint","IMPRINT",EDGE,{"derivedFrom":sQuery(id+"F1.wireOp",EDGE,"E75.0")}),-1.0]])]});
            var Q79;
            Q79=makeQuery(id+"F1.imprint","IMPRINT",FACE,{"disambiguationData":[TD([[makeQuery(id+"F1.imprint","IMPRINT",EDGE,{"derivedFrom":sQuery(id+"F1.wireOp",EDGE,"E234.0")}),1.0]])]});
            var Q80;
            Q80=makeQuery(id+"F1.imprint","IMPRINT",FACE,{"disambiguationData":[TD([[makeQuery(id+"F1.imprint","IMPRINT",EDGE,{"derivedFrom":sQuery(id+"F1.wireOp",EDGE,"E166.0")}),1.0]])]});
            var Q81;
            Q81=makeQuery(id+"F1.imprint","IMPRINT",FACE,{"disambiguationData":[TD([[makeQuery(id+"F1.imprint","IMPRINT",EDGE,{"derivedFrom":sQuery(id+"F1.wireOp",EDGE,"E233.0")}),1.0]])]});
            var Q82;
            Q82=makeQuery(id+"F1.imprint","IMPRINT",FACE,{"disambiguationData":[TD([[makeQuery(id+"F1.imprint","IMPRINT",EDGE,{"derivedFrom":sQuery(id+"F1.wireOp",EDGE,"E111.0")}),-1.0]])]});
            var Q83;
            Q83=makeQuery(id+"F1.imprint","IMPRINT",FACE,{"disambiguationData":[TD([[makeQuery(id+"F1.imprint","IMPRINT",EDGE,{"derivedFrom":sQuery(id+"F1.wireOp",EDGE,"E72.0")}),-1.0]])]});
            var Q84;
            Q84=makeQuery(id+"F1.imprint","IMPRINT",FACE,{"disambiguationData":[TD([[makeQuery(id+"F1.imprint","IMPRINT",EDGE,{"derivedFrom":sQuery(id+"F1.wireOp",EDGE,"E159.0")}),-1.0]])]});
            var Q85;
            Q85=makeQuery(id+"F1.imprint","IMPRINT",FACE,{"disambiguationData":[TD([[makeQuery(id+"F1.imprint","IMPRINT",EDGE,{"derivedFrom":sQuery(id+"F1.wireOp",EDGE,"E248.0")}),1.0]])]});
            var Q86;
            Q86=makeQuery(id+"F1.imprint","IMPRINT",FACE,{"disambiguationData":[TD([[makeQuery(id+"F1.imprint","IMPRINT",EDGE,{"derivedFrom":sQuery(id+"F1.wireOp",EDGE,"E182.0")}),1.0]])]});
            var Q87;
            Q87=makeQuery(id+"F1.imprint","IMPRINT",FACE,{"disambiguationData":[TD([[makeQuery(id+"F1.imprint","IMPRINT",EDGE,{"derivedFrom":sQuery(id+"F1.wireOp",EDGE,"E99.0")}),1.0]])]});
            var Q88;
            Q88=makeQuery(id+"F1.imprint","IMPRINT",FACE,{"disambiguationData":[TD([[makeQuery(id+"F1.imprint","IMPRINT",EDGE,{"derivedFrom":sQuery(id+"F1.wireOp",EDGE,"E71.0")}),1.0]])]});
            var Q89;
            Q89=makeQuery(id+"F1.imprint","IMPRINT",FACE,{"disambiguationData":[TD([[makeQuery(id+"F1.imprint","IMPRINT",EDGE,{"derivedFrom":sQuery(id+"F1.wireOp",EDGE,"E118.0")}),-1.0]])]});
            var Q90;
            Q90=makeQuery(id+"F1.imprint","IMPRINT",FACE,{"disambiguationData":[TD([[makeQuery(id+"F1.imprint","IMPRINT",EDGE,{"derivedFrom":sQuery(id+"F1.wireOp",EDGE,"E225.0")}),-1.0]])]});
            var Q91;
            Q91=makeQuery(id+"F1.imprint","IMPRINT",FACE,{"disambiguationData":[TD([[makeQuery(id+"F1.imprint","IMPRINT",EDGE,{"derivedFrom":sQuery(id+"F1.wireOp",EDGE,"E129.0")}),1.0]])]});
            var Q92;
            Q92=makeQuery(id+"F1.imprint","IMPRINT",FACE,{"disambiguationData":[TD([[makeQuery(id+"F1.imprint","IMPRINT",EDGE,{"derivedFrom":sQuery(id+"F1.wireOp",EDGE,"E275.0")}),1.0]])]});
            var Q93;
            Q93=makeQuery(id+"F1.imprint","IMPRINT",FACE,{"disambiguationData":[TD([[makeQuery(id+"F1.imprint","IMPRINT",EDGE,{"derivedFrom":sQuery(id+"F1.wireOp",EDGE,"E279.0")}),1.0]])]});
            var Q94;
            Q94=makeQuery(id+"F1.imprint","IMPRINT",FACE,{"disambiguationData":[TD([[makeQuery(id+"F1.imprint","IMPRINT",EDGE,{"derivedFrom":sQuery(id+"F1.wireOp",EDGE,"E290")}),1.0]])]});
            extrude(context, id + "F3", {"entities" : qUnion([Q0, Q1, Q2, Q3, Q4, Q5, Q6, Q7, Q8, Q9, Q10, Q11, Q12, Q13, Q14, Q15, Q16, Q17, Q18, Q19, Q20, Q21, Q22, Q23, Q24, Q25, Q26, Q27, Q28, Q29, Q30, Q31, Q32, Q33, Q34, Q35, Q36, Q37, Q38, Q39, Q40, Q41, Q42, Q43, Q44, Q45, Q46, Q47, Q48, Q49, Q50, Q51, Q52, Q53, Q54, Q55, Q56, Q57, Q58, Q59, Q60, Q61, Q62, Q63, Q64, Q65, Q66, Q67, Q68, Q69, Q70, Q71, Q72, Q73, Q74, Q75, Q76, Q77, Q78, Q79, Q80, Q81, Q82, Q83, Q84, Q85, Q86, Q87, Q88, Q89, Q90, Q91, Q92, Q93, Q94]), "operationType" : NewBodyOperationType.REMOVE, "depth" : 66.04 * mm, "offsetDistance" : 25.4 * mm});
        }
        {
            var Q0;
            Q0=makeQuery(id+"F2.opExtrude","SWEPT_BODY",BODY,{"disambiguationData":[OSD([sQuery(id+"F0.wireOp",EDGE,"E3"),sQuery(id+"F0.wireOp",EDGE,"E5"),sQuery(id+"F0.wireOp",EDGE,"E8"),sQuery(id+"F0.wireOp",EDGE,"E10")])]});
            var Q1;
            Q1=sQuery(id+"F0.wireOp",VERTEX,"E0.start");
            transform(context, id + "F4", {"entities" : qUnion([Q0]), "transformType" : TransformType.SCALE_UNIFORMLY, "scale" : .181, "scalePoint" : qUnion([Q1]), "makeCopy" : false});
        }
    });
